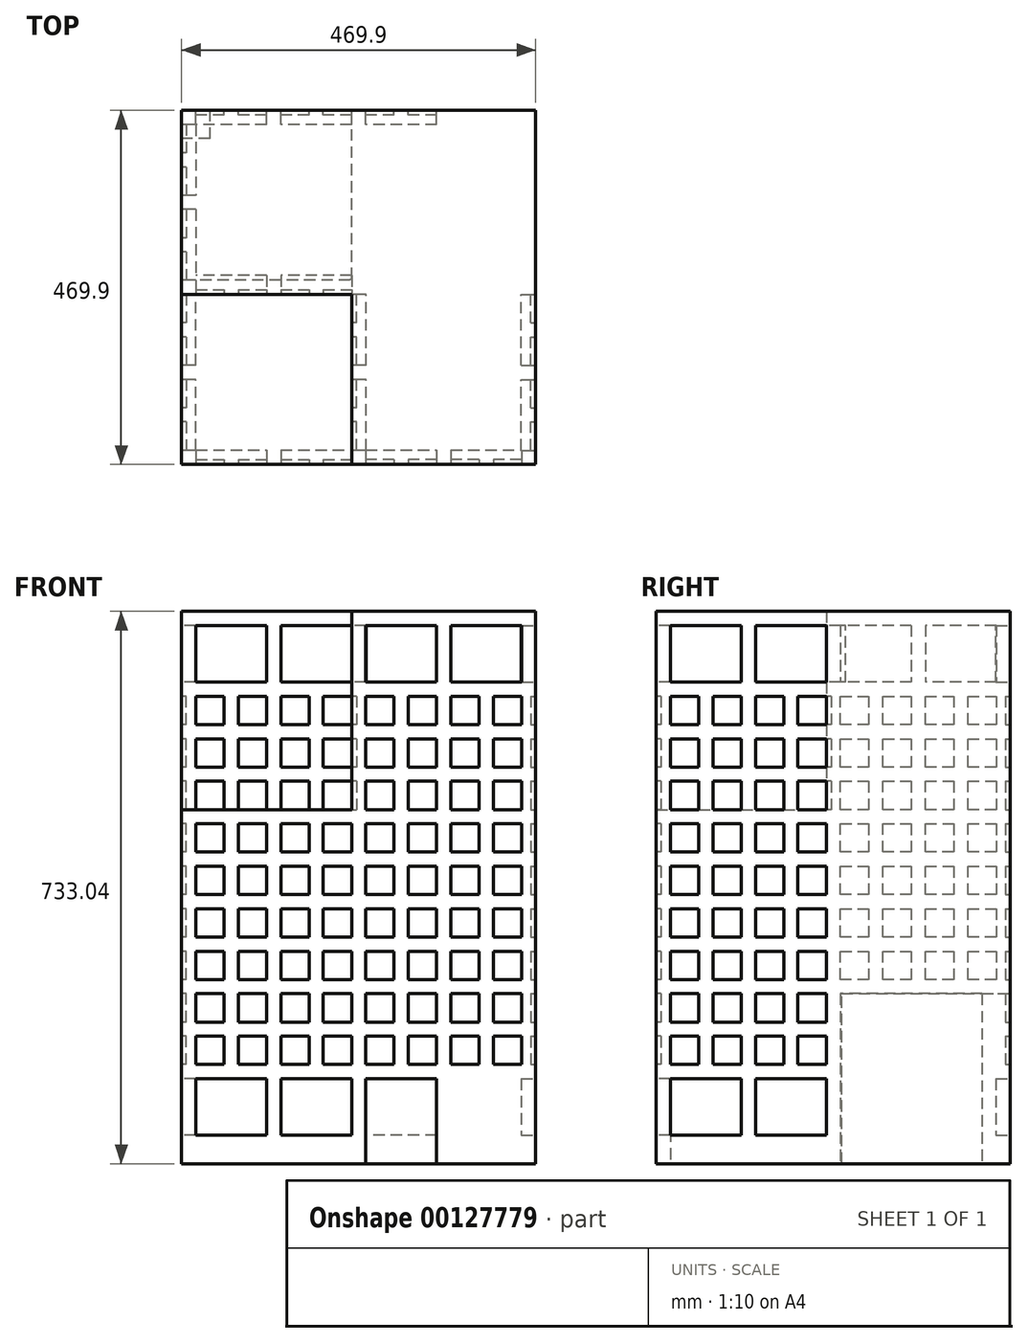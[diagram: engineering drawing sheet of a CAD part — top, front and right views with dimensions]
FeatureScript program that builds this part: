
annotation { "Feature Type Name" : "Feature", "Feature Type Description" : "" }
export const myFeature = defineFeature(function(context is Context, id is Id, definition is map)
    precondition{}
    {
        {
            var Q0;
            Q0=qCreatedBy(makeId("Front.planeOp"),FACE);
            var sketch = newSketch(context, id + "F0", { "sketchPlane" : qUnion([Q0])});
            skLineSegment(sketch, "E0", {"start": v(109.2, -466.79) * mm, "end": v(579.1, -466.79) * mm});
            skLineSegment(sketch, "E1", {"start": v(579.1, -466.79) * mm, "end": v(579.1, 303.85) * mm});
            skLineSegment(sketch, "E2", {"start": v(579.1, 303.85) * mm, "end": v(334.75, 303.85) * mm});
            skLineSegment(sketch, "E3", {"start": v(334.75, 303.85) * mm, "end": v(334.75, 21.9) * mm});
            skLineSegment(sketch, "E4", {"start": v(334.75, 21.9) * mm, "end": v(109.2, 21.9) * mm});
            skLineSegment(sketch, "E5", {"start": v(109.2, 21.9) * mm, "end": v(109.2, -466.79) * mm});
            skSolve(sketch);
        }
        {
            var Q0;
            {var subQ0=sQuery(id+"F0.wireOp",EDGE,"E1");Q0=makeQuery(id+"F0.imprint","IMPRINT",FACE,{"disambiguationData":[TD([[makeQuery(id+"F0.imprint","IMPRINT",EDGE,{"derivedFrom":subQ0}),1.0]])]});}
            extrude(context, id + "F1", {"entities" : qUnion([Q0]), "depth" : 469.9 * mm});
        }
        {
            var Q0;
            Q0=makeQuery(id+"F1.opExtrude","SWEPT_FACE",FACE,{"disambiguationData":[OSD([sQuery(id+"F0.wireOp",EDGE,"E4")])]});
            var sketch = newSketch(context, id + "F2", { "sketchPlane" : qUnion([Q0])});
            skLineSegment(sketch, "E6", {"start": v(104.7, -244.35) * mm, "end": v(339.26, -244.35) * mm});
            skSolve(sketch);
        }
        {
            var Q0;
            {var subQ1=sQuery(id+"F0.wireOp",EDGE,"E4");var subQ6=makeQuery(id+"F1.opExtrude","CAP_EDGE",EDGE,{"disambiguationData":[OSD([subQ1])],"isStart":true});Q0=makeQuery(id+"F2.imprint","IMPRINT",FACE,{"disambiguationData":[TD([[makeQuery(id+"F2.imprint","IMPRINT",EDGE,{"derivedFrom":subQ6}),1.0]])]});}
            extrude(context, id + "F3", {"entities" : qUnion([Q0]), "operationType" : NewBodyOperationType.ADD, "depth" : 281.94 * mm});
        }
        {
            var Q0;
            Q0=makeQuery(id+"F1.opExtrude","CAP_FACE",FACE,{"disambiguationData":[OSD([sQuery(id+"F0.wireOp",EDGE,"E0"),sQuery(id+"F0.wireOp",EDGE,"E1"),sQuery(id+"F0.wireOp",EDGE,"E2"),sQuery(id+"F0.wireOp",EDGE,"E3"),sQuery(id+"F0.wireOp",EDGE,"E4"),sQuery(id+"F0.wireOp",EDGE,"E5")])],"isStart":false});
            var sketch = newSketch(context, id + "F4", { "sketchPlane" : qUnion([Q0])});
            skLineSegment(sketch, "E7.bottom", {"start": v(128, -335.22) * mm, "end": v(221.98, -335.22) * mm});
            skLineSegment(sketch, "E7.top", {"start": v(128, -410.4) * mm, "end": v(221.98, -410.4) * mm});
            skLineSegment(sketch, "E7.left", {"start": v(128, -335.22) * mm, "end": v(128, -410.4) * mm});
            skLineSegment(sketch, "E7.right", {"start": v(221.98, -335.22) * mm, "end": v(221.98, -410.4) * mm});
            skLineSegment(sketch, "E8.1.0.0", {"start": v(240.77, -335.22) * mm, "end": v(334.75, -335.22) * mm});
            skLineSegment(sketch, "E8.1.0.1", {"start": v(334.75, -335.22) * mm, "end": v(334.75, -410.4) * mm});
            skLineSegment(sketch, "E8.1.0.2", {"start": v(240.77, -410.4) * mm, "end": v(334.75, -410.4) * mm});
            skLineSegment(sketch, "E8.1.0.3", {"start": v(240.77, -335.22) * mm, "end": v(240.77, -410.4) * mm});
            skLineSegment(sketch, "E8.2.0.0", {"start": v(353.55, -335.22) * mm, "end": v(447.53, -335.22) * mm});
            skLineSegment(sketch, "E8.2.0.1", {"start": v(447.53, -335.22) * mm, "end": v(447.53, -410.4) * mm});
            skLineSegment(sketch, "E8.2.0.3", {"start": v(353.55, -335.22) * mm, "end": v(353.55, -410.4) * mm});
            skLineSegment(sketch, "E8.direction1", {"start": v(128, -410.4) * mm, "end": v(240.77, -410.4) * mm, "construction": true});
            skLineSegment(sketch, "E9.bottom", {"start": v(522.71, -278.83) * mm, "end": v(560.3, -278.83) * mm});
            skLineSegment(sketch, "E9.top", {"start": v(522.71, -316.42) * mm, "end": v(560.3, -316.42) * mm});
            skLineSegment(sketch, "E9.left", {"start": v(522.71, -278.83) * mm, "end": v(522.71, -316.42) * mm});
            skLineSegment(sketch, "E9.right", {"start": v(560.3, -278.83) * mm, "end": v(560.3, -316.42) * mm});
            skLineSegment(sketch, "E10.0.1.0", {"start": v(522.71, -222.44) * mm, "end": v(560.3, -222.44) * mm});
            skLineSegment(sketch, "E10.0.1.1", {"start": v(560.3, -222.44) * mm, "end": v(560.3, -260.03) * mm});
            skLineSegment(sketch, "E10.0.1.2", {"start": v(522.71, -260.03) * mm, "end": v(560.3, -260.03) * mm});
            skLineSegment(sketch, "E10.0.1.3", {"start": v(522.71, -222.44) * mm, "end": v(522.71, -260.03) * mm});
            skLineSegment(sketch, "E10.0.2.0", {"start": v(522.71, -166.05) * mm, "end": v(560.3, -166.05) * mm});
            skLineSegment(sketch, "E10.0.2.1", {"start": v(560.3, -166.05) * mm, "end": v(560.3, -203.64) * mm});
            skLineSegment(sketch, "E10.0.2.2", {"start": v(522.71, -203.64) * mm, "end": v(560.3, -203.64) * mm});
            skLineSegment(sketch, "E10.0.2.3", {"start": v(522.71, -166.05) * mm, "end": v(522.71, -203.64) * mm});
            skLineSegment(sketch, "E10.0.3.0", {"start": v(522.71, -109.66) * mm, "end": v(560.3, -109.66) * mm});
            skLineSegment(sketch, "E10.0.3.1", {"start": v(560.3, -109.66) * mm, "end": v(560.3, -147.26) * mm});
            skLineSegment(sketch, "E10.0.3.2", {"start": v(522.71, -147.26) * mm, "end": v(560.3, -147.26) * mm});
            skLineSegment(sketch, "E10.0.3.3", {"start": v(522.71, -109.66) * mm, "end": v(522.71, -147.26) * mm});
            skLineSegment(sketch, "E10.0.4.0", {"start": v(522.71, -53.28) * mm, "end": v(560.3, -53.28) * mm});
            skLineSegment(sketch, "E10.0.4.1", {"start": v(560.3, -53.28) * mm, "end": v(560.3, -90.87) * mm});
            skLineSegment(sketch, "E10.0.4.2", {"start": v(522.71, -90.87) * mm, "end": v(560.3, -90.87) * mm});
            skLineSegment(sketch, "E10.0.4.3", {"start": v(522.71, -53.28) * mm, "end": v(522.71, -90.87) * mm});
            skLineSegment(sketch, "E10.0.5.0", {"start": v(522.71, 3.11) * mm, "end": v(560.3, 3.11) * mm});
            skLineSegment(sketch, "E10.0.5.1", {"start": v(560.3, 3.11) * mm, "end": v(560.3, -34.48) * mm});
            skLineSegment(sketch, "E10.0.5.2", {"start": v(522.71, -34.48) * mm, "end": v(560.3, -34.48) * mm});
            skLineSegment(sketch, "E10.0.5.3", {"start": v(522.71, 3.11) * mm, "end": v(522.71, -34.48) * mm});
            skLineSegment(sketch, "E10.1.0.0", {"start": v(466.33, -278.83) * mm, "end": v(503.92, -278.83) * mm});
            skLineSegment(sketch, "E10.1.0.1", {"start": v(503.92, -278.83) * mm, "end": v(503.92, -316.42) * mm});
            skLineSegment(sketch, "E10.1.0.2", {"start": v(466.33, -316.42) * mm, "end": v(503.92, -316.42) * mm});
            skLineSegment(sketch, "E10.1.0.3", {"start": v(466.33, -278.83) * mm, "end": v(466.33, -316.42) * mm});
            skLineSegment(sketch, "E10.1.1.0", {"start": v(466.33, -222.44) * mm, "end": v(503.92, -222.44) * mm});
            skLineSegment(sketch, "E10.1.1.1", {"start": v(503.92, -222.44) * mm, "end": v(503.92, -260.03) * mm});
            skLineSegment(sketch, "E10.1.1.2", {"start": v(466.33, -260.03) * mm, "end": v(503.92, -260.03) * mm});
            skLineSegment(sketch, "E10.1.1.3", {"start": v(466.33, -222.44) * mm, "end": v(466.33, -260.03) * mm});
            skLineSegment(sketch, "E10.1.2.0", {"start": v(466.33, -166.05) * mm, "end": v(503.92, -166.05) * mm});
            skLineSegment(sketch, "E10.1.2.1", {"start": v(503.92, -166.05) * mm, "end": v(503.92, -203.64) * mm});
            skLineSegment(sketch, "E10.1.2.2", {"start": v(466.33, -203.64) * mm, "end": v(503.92, -203.64) * mm});
            skLineSegment(sketch, "E10.1.2.3", {"start": v(466.33, -166.05) * mm, "end": v(466.33, -203.64) * mm});
            skLineSegment(sketch, "E10.1.3.0", {"start": v(466.33, -109.66) * mm, "end": v(503.92, -109.66) * mm});
            skLineSegment(sketch, "E10.1.3.1", {"start": v(503.92, -109.66) * mm, "end": v(503.92, -147.26) * mm});
            skLineSegment(sketch, "E10.1.3.2", {"start": v(466.33, -147.26) * mm, "end": v(503.92, -147.26) * mm});
            skLineSegment(sketch, "E10.1.3.3", {"start": v(466.33, -109.66) * mm, "end": v(466.33, -147.26) * mm});
            skLineSegment(sketch, "E10.1.4.0", {"start": v(466.33, -53.28) * mm, "end": v(503.92, -53.28) * mm});
            skLineSegment(sketch, "E10.1.4.1", {"start": v(503.92, -53.28) * mm, "end": v(503.92, -90.87) * mm});
            skLineSegment(sketch, "E10.1.4.2", {"start": v(466.33, -90.87) * mm, "end": v(503.92, -90.87) * mm});
            skLineSegment(sketch, "E10.1.4.3", {"start": v(466.33, -53.28) * mm, "end": v(466.33, -90.87) * mm});
            skLineSegment(sketch, "E10.1.5.0", {"start": v(466.33, 3.11) * mm, "end": v(503.92, 3.11) * mm});
            skLineSegment(sketch, "E10.1.5.1", {"start": v(503.92, 3.11) * mm, "end": v(503.92, -34.48) * mm});
            skLineSegment(sketch, "E10.1.5.2", {"start": v(466.33, -34.48) * mm, "end": v(503.92, -34.48) * mm});
            skLineSegment(sketch, "E10.1.5.3", {"start": v(466.33, 3.11) * mm, "end": v(466.33, -34.48) * mm});
            skLineSegment(sketch, "E10.2.0.0", {"start": v(409.94, -278.83) * mm, "end": v(447.53, -278.83) * mm});
            skLineSegment(sketch, "E10.2.0.1", {"start": v(447.53, -278.83) * mm, "end": v(447.53, -316.42) * mm});
            skLineSegment(sketch, "E10.2.0.2", {"start": v(409.94, -316.42) * mm, "end": v(447.53, -316.42) * mm});
            skLineSegment(sketch, "E10.2.0.3", {"start": v(409.94, -278.83) * mm, "end": v(409.94, -316.42) * mm});
            skLineSegment(sketch, "E10.2.1.0", {"start": v(409.94, -222.44) * mm, "end": v(447.53, -222.44) * mm});
            skLineSegment(sketch, "E10.2.1.1", {"start": v(447.53, -222.44) * mm, "end": v(447.53, -260.03) * mm});
            skLineSegment(sketch, "E10.2.1.2", {"start": v(409.94, -260.03) * mm, "end": v(447.53, -260.03) * mm});
            skLineSegment(sketch, "E10.2.1.3", {"start": v(409.94, -222.44) * mm, "end": v(409.94, -260.03) * mm});
            skLineSegment(sketch, "E10.2.2.0", {"start": v(409.94, -166.05) * mm, "end": v(447.53, -166.05) * mm});
            skLineSegment(sketch, "E10.2.2.1", {"start": v(447.53, -166.05) * mm, "end": v(447.53, -203.64) * mm});
            skLineSegment(sketch, "E10.2.2.2", {"start": v(409.94, -203.64) * mm, "end": v(447.53, -203.64) * mm});
            skLineSegment(sketch, "E10.2.2.3", {"start": v(409.94, -166.05) * mm, "end": v(409.94, -203.64) * mm});
            skLineSegment(sketch, "E10.2.3.0", {"start": v(409.94, -109.66) * mm, "end": v(447.53, -109.66) * mm});
            skLineSegment(sketch, "E10.2.3.1", {"start": v(447.53, -109.66) * mm, "end": v(447.53, -147.26) * mm});
            skLineSegment(sketch, "E10.2.3.2", {"start": v(409.94, -147.26) * mm, "end": v(447.53, -147.26) * mm});
            skLineSegment(sketch, "E10.2.3.3", {"start": v(409.94, -109.66) * mm, "end": v(409.94, -147.26) * mm});
            skLineSegment(sketch, "E10.2.4.0", {"start": v(409.94, -53.28) * mm, "end": v(447.53, -53.28) * mm});
            skLineSegment(sketch, "E10.2.4.1", {"start": v(447.53, -53.28) * mm, "end": v(447.53, -90.87) * mm});
            skLineSegment(sketch, "E10.2.4.2", {"start": v(409.94, -90.87) * mm, "end": v(447.53, -90.87) * mm});
            skLineSegment(sketch, "E10.2.4.3", {"start": v(409.94, -53.28) * mm, "end": v(409.94, -90.87) * mm});
            skLineSegment(sketch, "E10.2.5.0", {"start": v(409.94, 3.11) * mm, "end": v(447.53, 3.11) * mm});
            skLineSegment(sketch, "E10.2.5.1", {"start": v(447.53, 3.11) * mm, "end": v(447.53, -34.48) * mm});
            skLineSegment(sketch, "E10.2.5.2", {"start": v(409.94, -34.48) * mm, "end": v(447.53, -34.48) * mm});
            skLineSegment(sketch, "E10.2.5.3", {"start": v(409.94, 3.11) * mm, "end": v(409.94, -34.48) * mm});
            skLineSegment(sketch, "E10.3.0.0", {"start": v(353.55, -278.83) * mm, "end": v(391.14, -278.83) * mm});
            skLineSegment(sketch, "E10.3.0.1", {"start": v(391.14, -278.83) * mm, "end": v(391.14, -316.42) * mm});
            skLineSegment(sketch, "E10.3.0.2", {"start": v(353.55, -316.42) * mm, "end": v(391.14, -316.42) * mm});
            skLineSegment(sketch, "E10.3.0.3", {"start": v(353.55, -278.83) * mm, "end": v(353.55, -316.42) * mm});
            skLineSegment(sketch, "E10.3.1.0", {"start": v(353.55, -222.44) * mm, "end": v(391.14, -222.44) * mm});
            skLineSegment(sketch, "E10.3.1.1", {"start": v(391.14, -222.44) * mm, "end": v(391.14, -260.03) * mm});
            skLineSegment(sketch, "E10.3.1.2", {"start": v(353.55, -260.03) * mm, "end": v(391.14, -260.03) * mm});
            skLineSegment(sketch, "E10.3.1.3", {"start": v(353.55, -222.44) * mm, "end": v(353.55, -260.03) * mm});
            skLineSegment(sketch, "E10.3.2.0", {"start": v(353.55, -166.05) * mm, "end": v(391.14, -166.05) * mm});
            skLineSegment(sketch, "E10.3.2.1", {"start": v(391.14, -166.05) * mm, "end": v(391.14, -203.64) * mm});
            skLineSegment(sketch, "E10.3.2.2", {"start": v(353.55, -203.64) * mm, "end": v(391.14, -203.64) * mm});
            skLineSegment(sketch, "E10.3.2.3", {"start": v(353.55, -166.05) * mm, "end": v(353.55, -203.64) * mm});
            skLineSegment(sketch, "E10.3.3.0", {"start": v(353.55, -109.66) * mm, "end": v(391.14, -109.66) * mm});
            skLineSegment(sketch, "E10.3.3.1", {"start": v(391.14, -109.66) * mm, "end": v(391.14, -147.26) * mm});
            skLineSegment(sketch, "E10.3.3.2", {"start": v(353.55, -147.26) * mm, "end": v(391.14, -147.26) * mm});
            skLineSegment(sketch, "E10.3.3.3", {"start": v(353.55, -109.66) * mm, "end": v(353.55, -147.26) * mm});
            skLineSegment(sketch, "E10.3.4.0", {"start": v(353.55, -53.28) * mm, "end": v(391.14, -53.28) * mm});
            skLineSegment(sketch, "E10.3.4.1", {"start": v(391.14, -53.28) * mm, "end": v(391.14, -90.87) * mm});
            skLineSegment(sketch, "E10.3.4.2", {"start": v(353.55, -90.87) * mm, "end": v(391.14, -90.87) * mm});
            skLineSegment(sketch, "E10.3.4.3", {"start": v(353.55, -53.28) * mm, "end": v(353.55, -90.87) * mm});
            skLineSegment(sketch, "E10.3.5.0", {"start": v(353.55, 3.11) * mm, "end": v(391.14, 3.11) * mm});
            skLineSegment(sketch, "E10.3.5.1", {"start": v(391.14, 3.11) * mm, "end": v(391.14, -34.48) * mm});
            skLineSegment(sketch, "E10.3.5.2", {"start": v(353.55, -34.48) * mm, "end": v(391.14, -34.48) * mm});
            skLineSegment(sketch, "E10.3.5.3", {"start": v(353.55, 3.11) * mm, "end": v(353.55, -34.48) * mm});
            skLineSegment(sketch, "E10.4.0.0", {"start": v(297.16, -278.83) * mm, "end": v(334.75, -278.83) * mm});
            skLineSegment(sketch, "E10.4.0.1", {"start": v(334.75, -278.83) * mm, "end": v(334.75, -316.42) * mm});
            skLineSegment(sketch, "E10.4.0.2", {"start": v(297.16, -316.42) * mm, "end": v(334.75, -316.42) * mm});
            skLineSegment(sketch, "E10.4.0.3", {"start": v(297.16, -278.83) * mm, "end": v(297.16, -316.42) * mm});
            skLineSegment(sketch, "E10.4.1.0", {"start": v(297.16, -222.44) * mm, "end": v(334.75, -222.44) * mm});
            skLineSegment(sketch, "E10.4.1.1", {"start": v(334.75, -222.44) * mm, "end": v(334.75, -260.03) * mm});
            skLineSegment(sketch, "E10.4.1.2", {"start": v(297.16, -260.03) * mm, "end": v(334.75, -260.03) * mm});
            skLineSegment(sketch, "E10.4.1.3", {"start": v(297.16, -222.44) * mm, "end": v(297.16, -260.03) * mm});
            skLineSegment(sketch, "E10.4.2.0", {"start": v(297.16, -166.05) * mm, "end": v(334.75, -166.05) * mm});
            skLineSegment(sketch, "E10.4.2.1", {"start": v(334.75, -166.05) * mm, "end": v(334.75, -203.64) * mm});
            skLineSegment(sketch, "E10.4.2.2", {"start": v(297.16, -203.64) * mm, "end": v(334.75, -203.64) * mm});
            skLineSegment(sketch, "E10.4.2.3", {"start": v(297.16, -166.05) * mm, "end": v(297.16, -203.64) * mm});
            skLineSegment(sketch, "E10.4.3.0", {"start": v(297.16, -109.66) * mm, "end": v(334.75, -109.66) * mm});
            skLineSegment(sketch, "E10.4.3.1", {"start": v(334.75, -109.66) * mm, "end": v(334.75, -147.26) * mm});
            skLineSegment(sketch, "E10.4.3.2", {"start": v(297.16, -147.26) * mm, "end": v(334.75, -147.26) * mm});
            skLineSegment(sketch, "E10.4.3.3", {"start": v(297.16, -109.66) * mm, "end": v(297.16, -147.26) * mm});
            skLineSegment(sketch, "E10.4.4.0", {"start": v(297.16, -53.28) * mm, "end": v(334.75, -53.28) * mm});
            skLineSegment(sketch, "E10.4.4.1", {"start": v(334.75, -53.28) * mm, "end": v(334.75, -90.87) * mm});
            skLineSegment(sketch, "E10.4.4.2", {"start": v(297.16, -90.87) * mm, "end": v(334.75, -90.87) * mm});
            skLineSegment(sketch, "E10.4.4.3", {"start": v(297.16, -53.28) * mm, "end": v(297.16, -90.87) * mm});
            skLineSegment(sketch, "E10.4.5.0", {"start": v(297.16, 3.11) * mm, "end": v(334.75, 3.11) * mm});
            skLineSegment(sketch, "E10.4.5.1", {"start": v(334.75, 3.11) * mm, "end": v(334.75, -34.48) * mm});
            skLineSegment(sketch, "E10.4.5.2", {"start": v(297.16, -34.48) * mm, "end": v(334.75, -34.48) * mm});
            skLineSegment(sketch, "E10.4.5.3", {"start": v(297.16, 3.11) * mm, "end": v(297.16, -34.48) * mm});
            skLineSegment(sketch, "E10.5.0.0", {"start": v(240.77, -278.83) * mm, "end": v(278.37, -278.83) * mm});
            skLineSegment(sketch, "E10.5.0.1", {"start": v(278.37, -278.83) * mm, "end": v(278.37, -316.42) * mm});
            skLineSegment(sketch, "E10.5.0.2", {"start": v(240.77, -316.42) * mm, "end": v(278.37, -316.42) * mm});
            skLineSegment(sketch, "E10.5.0.3", {"start": v(240.77, -278.83) * mm, "end": v(240.77, -316.42) * mm});
            skLineSegment(sketch, "E10.5.1.0", {"start": v(240.77, -222.44) * mm, "end": v(278.37, -222.44) * mm});
            skLineSegment(sketch, "E10.5.1.1", {"start": v(278.37, -222.44) * mm, "end": v(278.37, -260.03) * mm});
            skLineSegment(sketch, "E10.5.1.2", {"start": v(240.77, -260.03) * mm, "end": v(278.37, -260.03) * mm});
            skLineSegment(sketch, "E10.5.1.3", {"start": v(240.77, -222.44) * mm, "end": v(240.77, -260.03) * mm});
            skLineSegment(sketch, "E10.5.2.0", {"start": v(240.77, -166.05) * mm, "end": v(278.37, -166.05) * mm});
            skLineSegment(sketch, "E10.5.2.1", {"start": v(278.37, -166.05) * mm, "end": v(278.37, -203.64) * mm});
            skLineSegment(sketch, "E10.5.2.2", {"start": v(240.77, -203.64) * mm, "end": v(278.37, -203.64) * mm});
            skLineSegment(sketch, "E10.5.2.3", {"start": v(240.77, -166.05) * mm, "end": v(240.77, -203.64) * mm});
            skLineSegment(sketch, "E10.5.3.0", {"start": v(240.77, -109.66) * mm, "end": v(278.37, -109.66) * mm});
            skLineSegment(sketch, "E10.5.3.1", {"start": v(278.37, -109.66) * mm, "end": v(278.37, -147.26) * mm});
            skLineSegment(sketch, "E10.5.3.2", {"start": v(240.77, -147.26) * mm, "end": v(278.37, -147.26) * mm});
            skLineSegment(sketch, "E10.5.3.3", {"start": v(240.77, -109.66) * mm, "end": v(240.77, -147.26) * mm});
            skLineSegment(sketch, "E10.5.4.0", {"start": v(240.77, -53.28) * mm, "end": v(278.37, -53.28) * mm});
            skLineSegment(sketch, "E10.5.4.1", {"start": v(278.37, -53.28) * mm, "end": v(278.37, -90.87) * mm});
            skLineSegment(sketch, "E10.5.4.2", {"start": v(240.77, -90.87) * mm, "end": v(278.37, -90.87) * mm});
            skLineSegment(sketch, "E10.5.4.3", {"start": v(240.77, -53.28) * mm, "end": v(240.77, -90.87) * mm});
            skLineSegment(sketch, "E10.5.5.0", {"start": v(240.77, 3.11) * mm, "end": v(278.37, 3.11) * mm});
            skLineSegment(sketch, "E10.5.5.1", {"start": v(278.37, 3.11) * mm, "end": v(278.37, -34.48) * mm});
            skLineSegment(sketch, "E10.5.5.2", {"start": v(240.77, -34.48) * mm, "end": v(278.37, -34.48) * mm});
            skLineSegment(sketch, "E10.5.5.3", {"start": v(240.77, 3.11) * mm, "end": v(240.77, -34.48) * mm});
            skLineSegment(sketch, "E10.6.0.0", {"start": v(184.39, -278.83) * mm, "end": v(221.98, -278.83) * mm});
            skLineSegment(sketch, "E10.6.0.1", {"start": v(221.98, -278.83) * mm, "end": v(221.98, -316.42) * mm});
            skLineSegment(sketch, "E10.6.0.2", {"start": v(184.39, -316.42) * mm, "end": v(221.98, -316.42) * mm});
            skLineSegment(sketch, "E10.6.0.3", {"start": v(184.39, -278.83) * mm, "end": v(184.39, -316.42) * mm});
            skLineSegment(sketch, "E10.6.1.0", {"start": v(184.39, -222.44) * mm, "end": v(221.98, -222.44) * mm});
            skLineSegment(sketch, "E10.6.1.1", {"start": v(221.98, -222.44) * mm, "end": v(221.98, -260.03) * mm});
            skLineSegment(sketch, "E10.6.1.2", {"start": v(184.39, -260.03) * mm, "end": v(221.98, -260.03) * mm});
            skLineSegment(sketch, "E10.6.1.3", {"start": v(184.39, -222.44) * mm, "end": v(184.39, -260.03) * mm});
            skLineSegment(sketch, "E10.6.2.0", {"start": v(184.39, -166.05) * mm, "end": v(221.98, -166.05) * mm});
            skLineSegment(sketch, "E10.6.2.1", {"start": v(221.98, -166.05) * mm, "end": v(221.98, -203.64) * mm});
            skLineSegment(sketch, "E10.6.2.2", {"start": v(184.39, -203.64) * mm, "end": v(221.98, -203.64) * mm});
            skLineSegment(sketch, "E10.6.2.3", {"start": v(184.39, -166.05) * mm, "end": v(184.39, -203.64) * mm});
            skLineSegment(sketch, "E10.6.3.0", {"start": v(184.39, -109.66) * mm, "end": v(221.98, -109.66) * mm});
            skLineSegment(sketch, "E10.6.3.1", {"start": v(221.98, -109.66) * mm, "end": v(221.98, -147.26) * mm});
            skLineSegment(sketch, "E10.6.3.2", {"start": v(184.39, -147.26) * mm, "end": v(221.98, -147.26) * mm});
            skLineSegment(sketch, "E10.6.3.3", {"start": v(184.39, -109.66) * mm, "end": v(184.39, -147.26) * mm});
            skLineSegment(sketch, "E10.6.4.0", {"start": v(184.39, -53.28) * mm, "end": v(221.98, -53.28) * mm});
            skLineSegment(sketch, "E10.6.4.1", {"start": v(221.98, -53.28) * mm, "end": v(221.98, -90.87) * mm});
            skLineSegment(sketch, "E10.6.4.2", {"start": v(184.39, -90.87) * mm, "end": v(221.98, -90.87) * mm});
            skLineSegment(sketch, "E10.6.4.3", {"start": v(184.39, -53.28) * mm, "end": v(184.39, -90.87) * mm});
            skLineSegment(sketch, "E10.6.5.0", {"start": v(184.39, 3.11) * mm, "end": v(221.98, 3.11) * mm});
            skLineSegment(sketch, "E10.6.5.1", {"start": v(221.98, 3.11) * mm, "end": v(221.98, -34.48) * mm});
            skLineSegment(sketch, "E10.6.5.2", {"start": v(184.39, -34.48) * mm, "end": v(221.98, -34.48) * mm});
            skLineSegment(sketch, "E10.6.5.3", {"start": v(184.39, 3.11) * mm, "end": v(184.39, -34.48) * mm});
            skLineSegment(sketch, "E10.7.0.0", {"start": v(128, -278.83) * mm, "end": v(165.59, -278.83) * mm});
            skLineSegment(sketch, "E10.7.0.1", {"start": v(165.59, -278.83) * mm, "end": v(165.59, -316.42) * mm});
            skLineSegment(sketch, "E10.7.0.2", {"start": v(128, -316.42) * mm, "end": v(165.59, -316.42) * mm});
            skLineSegment(sketch, "E10.7.0.3", {"start": v(128, -278.83) * mm, "end": v(128, -316.42) * mm});
            skLineSegment(sketch, "E10.7.1.0", {"start": v(128, -222.44) * mm, "end": v(165.59, -222.44) * mm});
            skLineSegment(sketch, "E10.7.1.1", {"start": v(165.59, -222.44) * mm, "end": v(165.59, -260.03) * mm});
            skLineSegment(sketch, "E10.7.1.2", {"start": v(128, -260.03) * mm, "end": v(165.59, -260.03) * mm});
            skLineSegment(sketch, "E10.7.1.3", {"start": v(128, -222.44) * mm, "end": v(128, -260.03) * mm});
            skLineSegment(sketch, "E10.7.2.0", {"start": v(128, -166.05) * mm, "end": v(165.59, -166.05) * mm});
            skLineSegment(sketch, "E10.7.2.1", {"start": v(165.59, -166.05) * mm, "end": v(165.59, -203.64) * mm});
            skLineSegment(sketch, "E10.7.2.2", {"start": v(128, -203.64) * mm, "end": v(165.59, -203.64) * mm});
            skLineSegment(sketch, "E10.7.2.3", {"start": v(128, -166.05) * mm, "end": v(128, -203.64) * mm});
            skLineSegment(sketch, "E10.7.3.0", {"start": v(128, -109.66) * mm, "end": v(165.59, -109.66) * mm});
            skLineSegment(sketch, "E10.7.3.1", {"start": v(165.59, -109.66) * mm, "end": v(165.59, -147.26) * mm});
            skLineSegment(sketch, "E10.7.3.2", {"start": v(128, -147.26) * mm, "end": v(165.59, -147.26) * mm});
            skLineSegment(sketch, "E10.7.3.3", {"start": v(128, -109.66) * mm, "end": v(128, -147.26) * mm});
            skLineSegment(sketch, "E10.7.4.0", {"start": v(128, -53.28) * mm, "end": v(165.59, -53.28) * mm});
            skLineSegment(sketch, "E10.7.4.1", {"start": v(165.59, -53.28) * mm, "end": v(165.59, -90.87) * mm});
            skLineSegment(sketch, "E10.7.4.2", {"start": v(128, -90.87) * mm, "end": v(165.59, -90.87) * mm});
            skLineSegment(sketch, "E10.7.4.3", {"start": v(128, -53.28) * mm, "end": v(128, -90.87) * mm});
            skLineSegment(sketch, "E10.7.5.0", {"start": v(128, 3.11) * mm, "end": v(165.59, 3.11) * mm});
            skLineSegment(sketch, "E10.7.5.1", {"start": v(165.59, 3.11) * mm, "end": v(165.59, -34.48) * mm});
            skLineSegment(sketch, "E10.7.5.2", {"start": v(128, -34.48) * mm, "end": v(165.59, -34.48) * mm});
            skLineSegment(sketch, "E10.7.5.3", {"start": v(128, 3.11) * mm, "end": v(128, -34.48) * mm});
            skLineSegment(sketch, "E10.direction1", {"start": v(522.71, -316.42) * mm, "end": v(466.33, -316.42) * mm, "construction": true});
            skLineSegment(sketch, "E10.direction2", {"start": v(522.71, -316.42) * mm, "end": v(522.71, -260.03) * mm, "construction": true});
            skLineSegment(sketch, "E11.bottom", {"start": v(466.33, 266.26) * mm, "end": v(560.3, 266.26) * mm});
            skLineSegment(sketch, "E11.top", {"start": v(466.33, 191.07) * mm, "end": v(560.3, 191.07) * mm});
            skLineSegment(sketch, "E11.left", {"start": v(466.33, 266.26) * mm, "end": v(466.33, 191.07) * mm});
            skLineSegment(sketch, "E11.right", {"start": v(560.3, 266.26) * mm, "end": v(560.3, 191.07) * mm});
            skLineSegment(sketch, "E12.bottom", {"start": v(353.55, 266.26) * mm, "end": v(447.53, 266.26) * mm});
            skLineSegment(sketch, "E12.top", {"start": v(353.55, 191.07) * mm, "end": v(447.53, 191.07) * mm});
            skLineSegment(sketch, "E12.left", {"start": v(353.55, 266.26) * mm, "end": v(353.55, 191.07) * mm});
            skLineSegment(sketch, "E12.right", {"start": v(447.53, 266.26) * mm, "end": v(447.53, 191.07) * mm});
            skLineSegment(sketch, "E13.bottom", {"start": v(560.3, 59.5) * mm, "end": v(522.71, 59.5) * mm});
            skLineSegment(sketch, "E13.top", {"start": v(560.3, 21.9) * mm, "end": v(522.71, 21.9) * mm});
            skLineSegment(sketch, "E13.left", {"start": v(560.3, 59.5) * mm, "end": v(560.3, 21.9) * mm});
            skLineSegment(sketch, "E13.right", {"start": v(522.71, 59.5) * mm, "end": v(522.71, 21.9) * mm});
            skLineSegment(sketch, "E14.0.1.0", {"start": v(560.3, 115.89) * mm, "end": v(522.71, 115.89) * mm});
            skLineSegment(sketch, "E14.0.1.1", {"start": v(560.3, 115.89) * mm, "end": v(560.3, 78.3) * mm});
            skLineSegment(sketch, "E14.0.1.2", {"start": v(560.3, 78.3) * mm, "end": v(522.71, 78.3) * mm});
            skLineSegment(sketch, "E14.0.1.3", {"start": v(522.71, 115.89) * mm, "end": v(522.71, 78.3) * mm});
            skLineSegment(sketch, "E14.0.2.0", {"start": v(560.3, 172.28) * mm, "end": v(522.71, 172.28) * mm});
            skLineSegment(sketch, "E14.0.2.1", {"start": v(560.3, 172.28) * mm, "end": v(560.3, 134.68) * mm});
            skLineSegment(sketch, "E14.0.2.2", {"start": v(560.3, 134.68) * mm, "end": v(522.71, 134.68) * mm});
            skLineSegment(sketch, "E14.0.2.3", {"start": v(522.71, 172.28) * mm, "end": v(522.71, 134.68) * mm});
            skLineSegment(sketch, "E14.1.0.0", {"start": v(503.92, 59.5) * mm, "end": v(466.33, 59.5) * mm});
            skLineSegment(sketch, "E14.1.0.1", {"start": v(503.92, 59.5) * mm, "end": v(503.92, 21.9) * mm});
            skLineSegment(sketch, "E14.1.0.2", {"start": v(503.92, 21.9) * mm, "end": v(466.33, 21.9) * mm});
            skLineSegment(sketch, "E14.1.0.3", {"start": v(466.33, 59.5) * mm, "end": v(466.33, 21.9) * mm});
            skLineSegment(sketch, "E14.1.1.0", {"start": v(503.92, 115.89) * mm, "end": v(466.33, 115.89) * mm});
            skLineSegment(sketch, "E14.1.1.1", {"start": v(503.92, 115.89) * mm, "end": v(503.92, 78.3) * mm});
            skLineSegment(sketch, "E14.1.1.2", {"start": v(503.92, 78.3) * mm, "end": v(466.33, 78.3) * mm});
            skLineSegment(sketch, "E14.1.1.3", {"start": v(466.33, 115.89) * mm, "end": v(466.33, 78.3) * mm});
            skLineSegment(sketch, "E14.1.2.0", {"start": v(503.92, 172.28) * mm, "end": v(466.33, 172.28) * mm});
            skLineSegment(sketch, "E14.1.2.1", {"start": v(503.92, 172.28) * mm, "end": v(503.92, 134.68) * mm});
            skLineSegment(sketch, "E14.1.2.2", {"start": v(503.92, 134.68) * mm, "end": v(466.33, 134.68) * mm});
            skLineSegment(sketch, "E14.1.2.3", {"start": v(466.33, 172.28) * mm, "end": v(466.33, 134.68) * mm});
            skLineSegment(sketch, "E14.2.0.0", {"start": v(447.53, 59.5) * mm, "end": v(409.94, 59.5) * mm});
            skLineSegment(sketch, "E14.2.0.1", {"start": v(447.53, 59.5) * mm, "end": v(447.53, 21.9) * mm});
            skLineSegment(sketch, "E14.2.0.2", {"start": v(447.53, 21.9) * mm, "end": v(409.94, 21.9) * mm});
            skLineSegment(sketch, "E14.2.0.3", {"start": v(409.94, 59.5) * mm, "end": v(409.94, 21.9) * mm});
            skLineSegment(sketch, "E14.2.1.0", {"start": v(447.53, 115.89) * mm, "end": v(409.94, 115.89) * mm});
            skLineSegment(sketch, "E14.2.1.1", {"start": v(447.53, 115.89) * mm, "end": v(447.53, 78.3) * mm});
            skLineSegment(sketch, "E14.2.1.2", {"start": v(447.53, 78.3) * mm, "end": v(409.94, 78.3) * mm});
            skLineSegment(sketch, "E14.2.1.3", {"start": v(409.94, 115.89) * mm, "end": v(409.94, 78.3) * mm});
            skLineSegment(sketch, "E14.2.2.0", {"start": v(447.53, 172.28) * mm, "end": v(409.94, 172.28) * mm});
            skLineSegment(sketch, "E14.2.2.1", {"start": v(447.53, 172.28) * mm, "end": v(447.53, 134.68) * mm});
            skLineSegment(sketch, "E14.2.2.2", {"start": v(447.53, 134.68) * mm, "end": v(409.94, 134.68) * mm});
            skLineSegment(sketch, "E14.2.2.3", {"start": v(409.94, 172.28) * mm, "end": v(409.94, 134.68) * mm});
            skLineSegment(sketch, "E14.3.0.0", {"start": v(391.14, 59.5) * mm, "end": v(353.55, 59.5) * mm});
            skLineSegment(sketch, "E14.3.0.1", {"start": v(391.14, 59.5) * mm, "end": v(391.14, 21.9) * mm});
            skLineSegment(sketch, "E14.3.0.2", {"start": v(391.14, 21.9) * mm, "end": v(353.55, 21.9) * mm});
            skLineSegment(sketch, "E14.3.0.3", {"start": v(353.55, 59.5) * mm, "end": v(353.55, 21.9) * mm});
            skLineSegment(sketch, "E14.3.1.0", {"start": v(391.14, 115.89) * mm, "end": v(353.55, 115.89) * mm});
            skLineSegment(sketch, "E14.3.1.1", {"start": v(391.14, 115.89) * mm, "end": v(391.14, 78.3) * mm});
            skLineSegment(sketch, "E14.3.1.2", {"start": v(391.14, 78.3) * mm, "end": v(353.55, 78.3) * mm});
            skLineSegment(sketch, "E14.3.1.3", {"start": v(353.55, 115.89) * mm, "end": v(353.55, 78.3) * mm});
            skLineSegment(sketch, "E14.3.2.0", {"start": v(391.14, 172.28) * mm, "end": v(353.55, 172.28) * mm});
            skLineSegment(sketch, "E14.3.2.1", {"start": v(391.14, 172.28) * mm, "end": v(391.14, 134.68) * mm});
            skLineSegment(sketch, "E14.3.2.2", {"start": v(391.14, 134.68) * mm, "end": v(353.55, 134.68) * mm});
            skLineSegment(sketch, "E14.3.2.3", {"start": v(353.55, 172.28) * mm, "end": v(353.55, 134.68) * mm});
            skLineSegment(sketch, "E14.direction1", {"start": v(522.71, 21.9) * mm, "end": v(466.33, 21.9) * mm, "construction": true});
            skLineSegment(sketch, "E14.direction2", {"start": v(522.71, 21.9) * mm, "end": v(522.71, 78.3) * mm, "construction": true});
            skLineSegment(sketch, "E15", {"start": v(353.55, -410.4) * mm, "end": v(353.55, -466.79) * mm});
            skLineSegment(sketch, "E16", {"start": v(447.53, -410.4) * mm, "end": v(447.53, -466.79) * mm});
            skSolve(sketch);
        }
        {
            var Q0;
            Q0=makeQuery(id+"F4.imprint","IMPRINT",FACE,{"disambiguationData":[TD([[makeQuery(id+"F4.imprint","IMPRINT",EDGE,{"derivedFrom":sQuery(id+"F4.wireOp",EDGE,"E12.bottom")}),-1.0]])]});
            var Q1;
            Q1=makeQuery(id+"F4.imprint","IMPRINT",FACE,{"disambiguationData":[TD([[makeQuery(id+"F4.imprint","IMPRINT",EDGE,{"derivedFrom":sQuery(id+"F4.wireOp",EDGE,"E11.bottom")}),-1.0]])]});
            var Q2;
            Q2=makeQuery(id+"F4.imprint","IMPRINT",FACE,{"disambiguationData":[TD([[makeQuery(id+"F4.imprint","IMPRINT",EDGE,{"derivedFrom":sQuery(id+"F4.wireOp",EDGE,"E8.2.0.0")}),-1.0]])]});
            var Q3;
            Q3=makeQuery(id+"F4.imprint","IMPRINT",FACE,{"disambiguationData":[TD([[makeQuery(id+"F4.imprint","IMPRINT",EDGE,{"derivedFrom":sQuery(id+"F4.wireOp",EDGE,"E8.1.0.0")}),-1.0]])]});
            var Q4;
            Q4=makeQuery(id+"F4.imprint","IMPRINT",FACE,{"disambiguationData":[TD([[makeQuery(id+"F4.imprint","IMPRINT",EDGE,{"derivedFrom":sQuery(id+"F4.wireOp",EDGE,"E7.bottom")}),-1.0]])]});
            extrude(context, id + "F5", {"entities" : qUnion([Q0, Q1, Q2, Q3, Q4]), "operationType" : NewBodyOperationType.REMOVE, "oppositeDirection" : true, "depth" : 19.05 * mm});
        }
        {
            var Q0;
            Q0 = qSketchRegion(id + "F4", true);
            extrude(context, id + "F6", {"entities" : qUnion([Q0]), "operationType" : NewBodyOperationType.REMOVE, "oppositeDirection" : true, "depth" : 6.35 * mm});
        }
        {
            var Q0;
            Q0=makeQuery(id+"F1.opExtrude","CAP_FACE",FACE,{"disambiguationData":[OSD([sQuery(id+"F0.wireOp",EDGE,"E0"),sQuery(id+"F0.wireOp",EDGE,"E1"),sQuery(id+"F0.wireOp",EDGE,"E2"),sQuery(id+"F0.wireOp",EDGE,"E3"),sQuery(id+"F0.wireOp",EDGE,"E4"),sQuery(id+"F0.wireOp",EDGE,"E5")])],"isStart":true});
            var sketch = newSketch(context, id + "F7", { "sketchPlane" : qUnion([Q0])});
            skLineSegment(sketch, "E17.bottom", {"start": v(-146.8, -466.79) * mm, "end": v(-334.75, -466.79) * mm});
            skLineSegment(sketch, "E17.top", {"start": v(-146.8, -222.44) * mm, "end": v(-334.75, -222.44) * mm});
            skLineSegment(sketch, "E17.left", {"start": v(-146.8, -466.79) * mm, "end": v(-146.8, -222.44) * mm});
            skLineSegment(sketch, "E17.right", {"start": v(-334.75, -466.79) * mm, "end": v(-334.75, -222.44) * mm});
            skLineSegment(sketch, "E18.bottom", {"start": v(-447.53, -335.22) * mm, "end": v(-353.55, -335.22) * mm});
            skLineSegment(sketch, "E18.top", {"start": v(-447.53, -410.4) * mm, "end": v(-353.55, -410.4) * mm});
            skLineSegment(sketch, "E18.left", {"start": v(-447.53, -335.22) * mm, "end": v(-447.53, -410.4) * mm});
            skLineSegment(sketch, "E18.right", {"start": v(-353.55, -335.22) * mm, "end": v(-353.55, -410.4) * mm});
            skLineSegment(sketch, "E19.bottom", {"start": v(-221.98, 266.26) * mm, "end": v(-128, 266.26) * mm});
            skLineSegment(sketch, "E19.top", {"start": v(-221.98, 191.07) * mm, "end": v(-128, 191.07) * mm});
            skLineSegment(sketch, "E19.left", {"start": v(-221.98, 266.26) * mm, "end": v(-221.98, 191.07) * mm});
            skLineSegment(sketch, "E19.right", {"start": v(-128, 266.26) * mm, "end": v(-128, 191.07) * mm});
            skLineSegment(sketch, "E20.bottom", {"start": v(-334.75, 266.26) * mm, "end": v(-240.77, 266.26) * mm});
            skLineSegment(sketch, "E20.top", {"start": v(-334.75, 191.07) * mm, "end": v(-240.77, 191.07) * mm});
            skLineSegment(sketch, "E20.left", {"start": v(-334.75, 266.26) * mm, "end": v(-334.75, 191.07) * mm});
            skLineSegment(sketch, "E20.right", {"start": v(-240.77, 266.26) * mm, "end": v(-240.77, 191.07) * mm});
            skLineSegment(sketch, "E21.bottom", {"start": v(-447.53, 266.26) * mm, "end": v(-353.55, 266.26) * mm});
            skLineSegment(sketch, "E21.top", {"start": v(-447.53, 191.07) * mm, "end": v(-353.55, 191.07) * mm});
            skLineSegment(sketch, "E21.left", {"start": v(-447.53, 266.26) * mm, "end": v(-447.53, 191.07) * mm});
            skLineSegment(sketch, "E21.right", {"start": v(-353.55, 266.26) * mm, "end": v(-353.55, 191.07) * mm});
            skLineSegment(sketch, "E22.bottom", {"start": v(-165.59, 172.28) * mm, "end": v(-128, 172.28) * mm});
            skLineSegment(sketch, "E22.top", {"start": v(-165.59, 134.68) * mm, "end": v(-128, 134.68) * mm});
            skLineSegment(sketch, "E22.left", {"start": v(-165.59, 172.28) * mm, "end": v(-165.59, 134.68) * mm});
            skLineSegment(sketch, "E22.right", {"start": v(-128, 172.28) * mm, "end": v(-128, 134.68) * mm});
            skLineSegment(sketch, "E23.0.1.0", {"start": v(-128, 115.89) * mm, "end": v(-128, 78.3) * mm});
            skLineSegment(sketch, "E23.0.1.1", {"start": v(-165.59, 78.3) * mm, "end": v(-128, 78.3) * mm});
            skLineSegment(sketch, "E23.0.1.2", {"start": v(-165.59, 115.89) * mm, "end": v(-165.59, 78.3) * mm});
            skLineSegment(sketch, "E23.0.1.3", {"start": v(-165.59, 115.89) * mm, "end": v(-128, 115.89) * mm});
            skLineSegment(sketch, "E23.0.2.0", {"start": v(-128, 59.5) * mm, "end": v(-128, 21.9) * mm});
            skLineSegment(sketch, "E23.0.2.1", {"start": v(-165.59, 21.9) * mm, "end": v(-128, 21.9) * mm});
            skLineSegment(sketch, "E23.0.2.2", {"start": v(-165.59, 59.5) * mm, "end": v(-165.59, 21.9) * mm});
            skLineSegment(sketch, "E23.0.2.3", {"start": v(-165.59, 59.5) * mm, "end": v(-128, 59.5) * mm});
            skLineSegment(sketch, "E23.0.3.0", {"start": v(-128, 3.11) * mm, "end": v(-128, -34.48) * mm});
            skLineSegment(sketch, "E23.0.3.1", {"start": v(-165.59, -34.48) * mm, "end": v(-128, -34.48) * mm});
            skLineSegment(sketch, "E23.0.3.2", {"start": v(-165.59, 3.11) * mm, "end": v(-165.59, -34.48) * mm});
            skLineSegment(sketch, "E23.0.3.3", {"start": v(-165.59, 3.11) * mm, "end": v(-128, 3.11) * mm});
            skLineSegment(sketch, "E23.0.4.0", {"start": v(-128, -53.28) * mm, "end": v(-128, -90.87) * mm});
            skLineSegment(sketch, "E23.0.4.1", {"start": v(-165.59, -90.87) * mm, "end": v(-128, -90.87) * mm});
            skLineSegment(sketch, "E23.0.4.2", {"start": v(-165.59, -53.28) * mm, "end": v(-165.59, -90.87) * mm});
            skLineSegment(sketch, "E23.0.4.3", {"start": v(-165.59, -53.28) * mm, "end": v(-128, -53.28) * mm});
            skLineSegment(sketch, "E23.0.5.0", {"start": v(-128, -109.66) * mm, "end": v(-128, -147.26) * mm});
            skLineSegment(sketch, "E23.0.5.1", {"start": v(-165.59, -147.26) * mm, "end": v(-128, -147.26) * mm});
            skLineSegment(sketch, "E23.0.5.2", {"start": v(-165.59, -109.66) * mm, "end": v(-165.59, -147.26) * mm});
            skLineSegment(sketch, "E23.0.5.3", {"start": v(-165.59, -109.66) * mm, "end": v(-128, -109.66) * mm});
            skLineSegment(sketch, "E23.0.6.0", {"start": v(-128, -166.05) * mm, "end": v(-128, -203.64) * mm});
            skLineSegment(sketch, "E23.0.6.1", {"start": v(-165.59, -203.64) * mm, "end": v(-128, -203.64) * mm});
            skLineSegment(sketch, "E23.0.6.2", {"start": v(-165.59, -166.05) * mm, "end": v(-165.59, -203.64) * mm});
            skLineSegment(sketch, "E23.0.6.3", {"start": v(-165.59, -166.05) * mm, "end": v(-128, -166.05) * mm});
            skLineSegment(sketch, "E23.1.0.0", {"start": v(-184.39, 172.28) * mm, "end": v(-184.39, 134.68) * mm});
            skLineSegment(sketch, "E23.1.0.1", {"start": v(-221.98, 134.68) * mm, "end": v(-184.39, 134.68) * mm});
            skLineSegment(sketch, "E23.1.0.2", {"start": v(-221.98, 172.28) * mm, "end": v(-221.98, 134.68) * mm});
            skLineSegment(sketch, "E23.1.0.3", {"start": v(-221.98, 172.28) * mm, "end": v(-184.39, 172.28) * mm});
            skLineSegment(sketch, "E23.1.1.0", {"start": v(-184.39, 115.89) * mm, "end": v(-184.39, 78.3) * mm});
            skLineSegment(sketch, "E23.1.1.1", {"start": v(-221.98, 78.3) * mm, "end": v(-184.39, 78.3) * mm});
            skLineSegment(sketch, "E23.1.1.2", {"start": v(-221.98, 115.89) * mm, "end": v(-221.98, 78.3) * mm});
            skLineSegment(sketch, "E23.1.1.3", {"start": v(-221.98, 115.89) * mm, "end": v(-184.39, 115.89) * mm});
            skLineSegment(sketch, "E23.1.2.0", {"start": v(-184.39, 59.5) * mm, "end": v(-184.39, 21.9) * mm});
            skLineSegment(sketch, "E23.1.2.1", {"start": v(-221.98, 21.9) * mm, "end": v(-184.39, 21.9) * mm});
            skLineSegment(sketch, "E23.1.2.2", {"start": v(-221.98, 59.5) * mm, "end": v(-221.98, 21.9) * mm});
            skLineSegment(sketch, "E23.1.2.3", {"start": v(-221.98, 59.5) * mm, "end": v(-184.39, 59.5) * mm});
            skLineSegment(sketch, "E23.1.3.0", {"start": v(-184.39, 3.11) * mm, "end": v(-184.39, -34.48) * mm});
            skLineSegment(sketch, "E23.1.3.1", {"start": v(-221.98, -34.48) * mm, "end": v(-184.39, -34.48) * mm});
            skLineSegment(sketch, "E23.1.3.2", {"start": v(-221.98, 3.11) * mm, "end": v(-221.98, -34.48) * mm});
            skLineSegment(sketch, "E23.1.3.3", {"start": v(-221.98, 3.11) * mm, "end": v(-184.39, 3.11) * mm});
            skLineSegment(sketch, "E23.1.4.0", {"start": v(-184.39, -53.28) * mm, "end": v(-184.39, -90.87) * mm});
            skLineSegment(sketch, "E23.1.4.1", {"start": v(-221.98, -90.87) * mm, "end": v(-184.39, -90.87) * mm});
            skLineSegment(sketch, "E23.1.4.2", {"start": v(-221.98, -53.28) * mm, "end": v(-221.98, -90.87) * mm});
            skLineSegment(sketch, "E23.1.4.3", {"start": v(-221.98, -53.28) * mm, "end": v(-184.39, -53.28) * mm});
            skLineSegment(sketch, "E23.1.5.0", {"start": v(-184.39, -109.66) * mm, "end": v(-184.39, -147.26) * mm});
            skLineSegment(sketch, "E23.1.5.1", {"start": v(-221.98, -147.26) * mm, "end": v(-184.39, -147.26) * mm});
            skLineSegment(sketch, "E23.1.5.2", {"start": v(-221.98, -109.66) * mm, "end": v(-221.98, -147.26) * mm});
            skLineSegment(sketch, "E23.1.5.3", {"start": v(-221.98, -109.66) * mm, "end": v(-184.39, -109.66) * mm});
            skLineSegment(sketch, "E23.1.6.0", {"start": v(-184.39, -166.05) * mm, "end": v(-184.39, -203.64) * mm});
            skLineSegment(sketch, "E23.1.6.1", {"start": v(-221.98, -203.64) * mm, "end": v(-184.39, -203.64) * mm});
            skLineSegment(sketch, "E23.1.6.2", {"start": v(-221.98, -166.05) * mm, "end": v(-221.98, -203.64) * mm});
            skLineSegment(sketch, "E23.1.6.3", {"start": v(-221.98, -166.05) * mm, "end": v(-184.39, -166.05) * mm});
            skLineSegment(sketch, "E23.2.0.0", {"start": v(-240.77, 172.28) * mm, "end": v(-240.77, 134.68) * mm});
            skLineSegment(sketch, "E23.2.0.1", {"start": v(-278.37, 134.68) * mm, "end": v(-240.77, 134.68) * mm});
            skLineSegment(sketch, "E23.2.0.2", {"start": v(-278.37, 172.28) * mm, "end": v(-278.37, 134.68) * mm});
            skLineSegment(sketch, "E23.2.0.3", {"start": v(-278.37, 172.28) * mm, "end": v(-240.77, 172.28) * mm});
            skLineSegment(sketch, "E23.2.1.0", {"start": v(-240.77, 115.89) * mm, "end": v(-240.77, 78.3) * mm});
            skLineSegment(sketch, "E23.2.1.1", {"start": v(-278.37, 78.3) * mm, "end": v(-240.77, 78.3) * mm});
            skLineSegment(sketch, "E23.2.1.2", {"start": v(-278.37, 115.89) * mm, "end": v(-278.37, 78.3) * mm});
            skLineSegment(sketch, "E23.2.1.3", {"start": v(-278.37, 115.89) * mm, "end": v(-240.77, 115.89) * mm});
            skLineSegment(sketch, "E23.2.2.0", {"start": v(-240.77, 59.5) * mm, "end": v(-240.77, 21.9) * mm});
            skLineSegment(sketch, "E23.2.2.1", {"start": v(-278.37, 21.9) * mm, "end": v(-240.77, 21.9) * mm});
            skLineSegment(sketch, "E23.2.2.2", {"start": v(-278.37, 59.5) * mm, "end": v(-278.37, 21.9) * mm});
            skLineSegment(sketch, "E23.2.2.3", {"start": v(-278.37, 59.5) * mm, "end": v(-240.77, 59.5) * mm});
            skLineSegment(sketch, "E23.2.3.0", {"start": v(-240.77, 3.11) * mm, "end": v(-240.77, -34.48) * mm});
            skLineSegment(sketch, "E23.2.3.1", {"start": v(-278.37, -34.48) * mm, "end": v(-240.77, -34.48) * mm});
            skLineSegment(sketch, "E23.2.3.2", {"start": v(-278.37, 3.11) * mm, "end": v(-278.37, -34.48) * mm});
            skLineSegment(sketch, "E23.2.3.3", {"start": v(-278.37, 3.11) * mm, "end": v(-240.77, 3.11) * mm});
            skLineSegment(sketch, "E23.2.4.0", {"start": v(-240.77, -53.28) * mm, "end": v(-240.77, -90.87) * mm});
            skLineSegment(sketch, "E23.2.4.1", {"start": v(-278.37, -90.87) * mm, "end": v(-240.77, -90.87) * mm});
            skLineSegment(sketch, "E23.2.4.2", {"start": v(-278.37, -53.28) * mm, "end": v(-278.37, -90.87) * mm});
            skLineSegment(sketch, "E23.2.4.3", {"start": v(-278.37, -53.28) * mm, "end": v(-240.77, -53.28) * mm});
            skLineSegment(sketch, "E23.2.5.0", {"start": v(-240.77, -109.66) * mm, "end": v(-240.77, -147.26) * mm});
            skLineSegment(sketch, "E23.2.5.1", {"start": v(-278.37, -147.26) * mm, "end": v(-240.77, -147.26) * mm});
            skLineSegment(sketch, "E23.2.5.2", {"start": v(-278.37, -109.66) * mm, "end": v(-278.37, -147.26) * mm});
            skLineSegment(sketch, "E23.2.5.3", {"start": v(-278.37, -109.66) * mm, "end": v(-240.77, -109.66) * mm});
            skLineSegment(sketch, "E23.2.6.0", {"start": v(-240.77, -166.05) * mm, "end": v(-240.77, -203.64) * mm});
            skLineSegment(sketch, "E23.2.6.1", {"start": v(-278.37, -203.64) * mm, "end": v(-240.77, -203.64) * mm});
            skLineSegment(sketch, "E23.2.6.2", {"start": v(-278.37, -166.05) * mm, "end": v(-278.37, -203.64) * mm});
            skLineSegment(sketch, "E23.2.6.3", {"start": v(-278.37, -166.05) * mm, "end": v(-240.77, -166.05) * mm});
            skLineSegment(sketch, "E23.3.0.0", {"start": v(-297.16, 172.28) * mm, "end": v(-297.16, 134.68) * mm});
            skLineSegment(sketch, "E23.3.0.1", {"start": v(-334.75, 134.68) * mm, "end": v(-297.16, 134.68) * mm});
            skLineSegment(sketch, "E23.3.0.2", {"start": v(-334.75, 172.28) * mm, "end": v(-334.75, 134.68) * mm});
            skLineSegment(sketch, "E23.3.0.3", {"start": v(-334.75, 172.28) * mm, "end": v(-297.16, 172.28) * mm});
            skLineSegment(sketch, "E23.3.1.0", {"start": v(-297.16, 115.89) * mm, "end": v(-297.16, 78.3) * mm});
            skLineSegment(sketch, "E23.3.1.1", {"start": v(-334.75, 78.3) * mm, "end": v(-297.16, 78.3) * mm});
            skLineSegment(sketch, "E23.3.1.2", {"start": v(-334.75, 115.89) * mm, "end": v(-334.75, 78.3) * mm});
            skLineSegment(sketch, "E23.3.1.3", {"start": v(-334.75, 115.89) * mm, "end": v(-297.16, 115.89) * mm});
            skLineSegment(sketch, "E23.3.2.0", {"start": v(-297.16, 59.5) * mm, "end": v(-297.16, 21.9) * mm});
            skLineSegment(sketch, "E23.3.2.1", {"start": v(-334.75, 21.9) * mm, "end": v(-297.16, 21.9) * mm});
            skLineSegment(sketch, "E23.3.2.2", {"start": v(-334.75, 59.5) * mm, "end": v(-334.75, 21.9) * mm});
            skLineSegment(sketch, "E23.3.2.3", {"start": v(-334.75, 59.5) * mm, "end": v(-297.16, 59.5) * mm});
            skLineSegment(sketch, "E23.3.3.0", {"start": v(-297.16, 3.11) * mm, "end": v(-297.16, -34.48) * mm});
            skLineSegment(sketch, "E23.3.3.1", {"start": v(-334.75, -34.48) * mm, "end": v(-297.16, -34.48) * mm});
            skLineSegment(sketch, "E23.3.3.2", {"start": v(-334.75, 3.11) * mm, "end": v(-334.75, -34.48) * mm});
            skLineSegment(sketch, "E23.3.3.3", {"start": v(-334.75, 3.11) * mm, "end": v(-297.16, 3.11) * mm});
            skLineSegment(sketch, "E23.3.4.0", {"start": v(-297.16, -53.28) * mm, "end": v(-297.16, -90.87) * mm});
            skLineSegment(sketch, "E23.3.4.1", {"start": v(-334.75, -90.87) * mm, "end": v(-297.16, -90.87) * mm});
            skLineSegment(sketch, "E23.3.4.2", {"start": v(-334.75, -53.28) * mm, "end": v(-334.75, -90.87) * mm});
            skLineSegment(sketch, "E23.3.4.3", {"start": v(-334.75, -53.28) * mm, "end": v(-297.16, -53.28) * mm});
            skLineSegment(sketch, "E23.3.5.0", {"start": v(-297.16, -109.66) * mm, "end": v(-297.16, -147.26) * mm});
            skLineSegment(sketch, "E23.3.5.1", {"start": v(-334.75, -147.26) * mm, "end": v(-297.16, -147.26) * mm});
            skLineSegment(sketch, "E23.3.5.2", {"start": v(-334.75, -109.66) * mm, "end": v(-334.75, -147.26) * mm});
            skLineSegment(sketch, "E23.3.5.3", {"start": v(-334.75, -109.66) * mm, "end": v(-297.16, -109.66) * mm});
            skLineSegment(sketch, "E23.3.6.0", {"start": v(-297.16, -166.05) * mm, "end": v(-297.16, -203.64) * mm});
            skLineSegment(sketch, "E23.3.6.1", {"start": v(-334.75, -203.64) * mm, "end": v(-297.16, -203.64) * mm});
            skLineSegment(sketch, "E23.3.6.2", {"start": v(-334.75, -166.05) * mm, "end": v(-334.75, -203.64) * mm});
            skLineSegment(sketch, "E23.3.6.3", {"start": v(-334.75, -166.05) * mm, "end": v(-297.16, -166.05) * mm});
            skLineSegment(sketch, "E23.4.0.0", {"start": v(-353.55, 172.28) * mm, "end": v(-353.55, 134.68) * mm});
            skLineSegment(sketch, "E23.4.0.1", {"start": v(-391.14, 134.68) * mm, "end": v(-353.55, 134.68) * mm});
            skLineSegment(sketch, "E23.4.0.2", {"start": v(-391.14, 172.28) * mm, "end": v(-391.14, 134.68) * mm});
            skLineSegment(sketch, "E23.4.0.3", {"start": v(-391.14, 172.28) * mm, "end": v(-353.55, 172.28) * mm});
            skLineSegment(sketch, "E23.4.1.0", {"start": v(-353.55, 115.89) * mm, "end": v(-353.55, 78.3) * mm});
            skLineSegment(sketch, "E23.4.1.1", {"start": v(-391.14, 78.3) * mm, "end": v(-353.55, 78.3) * mm});
            skLineSegment(sketch, "E23.4.1.2", {"start": v(-391.14, 115.89) * mm, "end": v(-391.14, 78.3) * mm});
            skLineSegment(sketch, "E23.4.1.3", {"start": v(-391.14, 115.89) * mm, "end": v(-353.55, 115.89) * mm});
            skLineSegment(sketch, "E23.4.2.0", {"start": v(-353.55, 59.5) * mm, "end": v(-353.55, 21.9) * mm});
            skLineSegment(sketch, "E23.4.2.1", {"start": v(-391.14, 21.9) * mm, "end": v(-353.55, 21.9) * mm});
            skLineSegment(sketch, "E23.4.2.2", {"start": v(-391.14, 59.5) * mm, "end": v(-391.14, 21.9) * mm});
            skLineSegment(sketch, "E23.4.2.3", {"start": v(-391.14, 59.5) * mm, "end": v(-353.55, 59.5) * mm});
            skLineSegment(sketch, "E23.4.3.0", {"start": v(-353.55, 3.11) * mm, "end": v(-353.55, -34.48) * mm});
            skLineSegment(sketch, "E23.4.3.1", {"start": v(-391.14, -34.48) * mm, "end": v(-353.55, -34.48) * mm});
            skLineSegment(sketch, "E23.4.3.2", {"start": v(-391.14, 3.11) * mm, "end": v(-391.14, -34.48) * mm});
            skLineSegment(sketch, "E23.4.3.3", {"start": v(-391.14, 3.11) * mm, "end": v(-353.55, 3.11) * mm});
            skLineSegment(sketch, "E23.4.4.0", {"start": v(-353.55, -53.28) * mm, "end": v(-353.55, -90.87) * mm});
            skLineSegment(sketch, "E23.4.4.1", {"start": v(-391.14, -90.87) * mm, "end": v(-353.55, -90.87) * mm});
            skLineSegment(sketch, "E23.4.4.2", {"start": v(-391.14, -53.28) * mm, "end": v(-391.14, -90.87) * mm});
            skLineSegment(sketch, "E23.4.4.3", {"start": v(-391.14, -53.28) * mm, "end": v(-353.55, -53.28) * mm});
            skLineSegment(sketch, "E23.4.5.0", {"start": v(-353.55, -109.66) * mm, "end": v(-353.55, -147.26) * mm});
            skLineSegment(sketch, "E23.4.5.1", {"start": v(-391.14, -147.26) * mm, "end": v(-353.55, -147.26) * mm});
            skLineSegment(sketch, "E23.4.5.2", {"start": v(-391.14, -109.66) * mm, "end": v(-391.14, -147.26) * mm});
            skLineSegment(sketch, "E23.4.5.3", {"start": v(-391.14, -109.66) * mm, "end": v(-353.55, -109.66) * mm});
            skLineSegment(sketch, "E23.4.6.0", {"start": v(-353.55, -166.05) * mm, "end": v(-353.55, -203.64) * mm});
            skLineSegment(sketch, "E23.4.6.1", {"start": v(-391.14, -203.64) * mm, "end": v(-353.55, -203.64) * mm});
            skLineSegment(sketch, "E23.4.6.2", {"start": v(-391.14, -166.05) * mm, "end": v(-391.14, -203.64) * mm});
            skLineSegment(sketch, "E23.4.6.3", {"start": v(-391.14, -166.05) * mm, "end": v(-353.55, -166.05) * mm});
            skLineSegment(sketch, "E23.4.7.0", {"start": v(-353.55, -222.44) * mm, "end": v(-353.55, -260.03) * mm});
            skLineSegment(sketch, "E23.4.7.1", {"start": v(-391.14, -260.03) * mm, "end": v(-353.55, -260.03) * mm});
            skLineSegment(sketch, "E23.4.7.2", {"start": v(-391.14, -222.44) * mm, "end": v(-391.14, -260.03) * mm});
            skLineSegment(sketch, "E23.4.7.3", {"start": v(-391.14, -222.44) * mm, "end": v(-353.55, -222.44) * mm});
            skLineSegment(sketch, "E23.4.8.0", {"start": v(-353.55, -278.83) * mm, "end": v(-353.55, -316.42) * mm});
            skLineSegment(sketch, "E23.4.8.1", {"start": v(-391.14, -316.42) * mm, "end": v(-353.55, -316.42) * mm});
            skLineSegment(sketch, "E23.4.8.2", {"start": v(-391.14, -278.83) * mm, "end": v(-391.14, -316.42) * mm});
            skLineSegment(sketch, "E23.4.8.3", {"start": v(-391.14, -278.83) * mm, "end": v(-353.55, -278.83) * mm});
            skLineSegment(sketch, "E23.5.0.0", {"start": v(-409.94, 172.28) * mm, "end": v(-409.94, 134.68) * mm});
            skLineSegment(sketch, "E23.5.0.1", {"start": v(-447.53, 134.68) * mm, "end": v(-409.94, 134.68) * mm});
            skLineSegment(sketch, "E23.5.0.2", {"start": v(-447.53, 172.28) * mm, "end": v(-447.53, 134.68) * mm});
            skLineSegment(sketch, "E23.5.0.3", {"start": v(-447.53, 172.28) * mm, "end": v(-409.94, 172.28) * mm});
            skLineSegment(sketch, "E23.5.1.0", {"start": v(-409.94, 115.89) * mm, "end": v(-409.94, 78.3) * mm});
            skLineSegment(sketch, "E23.5.1.1", {"start": v(-447.53, 78.3) * mm, "end": v(-409.94, 78.3) * mm});
            skLineSegment(sketch, "E23.5.1.2", {"start": v(-447.53, 115.89) * mm, "end": v(-447.53, 78.3) * mm});
            skLineSegment(sketch, "E23.5.1.3", {"start": v(-447.53, 115.89) * mm, "end": v(-409.94, 115.89) * mm});
            skLineSegment(sketch, "E23.5.2.0", {"start": v(-409.94, 59.5) * mm, "end": v(-409.94, 21.9) * mm});
            skLineSegment(sketch, "E23.5.2.1", {"start": v(-447.53, 21.9) * mm, "end": v(-409.94, 21.9) * mm});
            skLineSegment(sketch, "E23.5.2.2", {"start": v(-447.53, 59.5) * mm, "end": v(-447.53, 21.9) * mm});
            skLineSegment(sketch, "E23.5.2.3", {"start": v(-447.53, 59.5) * mm, "end": v(-409.94, 59.5) * mm});
            skLineSegment(sketch, "E23.5.3.0", {"start": v(-409.94, 3.11) * mm, "end": v(-409.94, -34.48) * mm});
            skLineSegment(sketch, "E23.5.3.1", {"start": v(-447.53, -34.48) * mm, "end": v(-409.94, -34.48) * mm});
            skLineSegment(sketch, "E23.5.3.2", {"start": v(-447.53, 3.11) * mm, "end": v(-447.53, -34.48) * mm});
            skLineSegment(sketch, "E23.5.3.3", {"start": v(-447.53, 3.11) * mm, "end": v(-409.94, 3.11) * mm});
            skLineSegment(sketch, "E23.5.4.0", {"start": v(-409.94, -53.28) * mm, "end": v(-409.94, -90.87) * mm});
            skLineSegment(sketch, "E23.5.4.1", {"start": v(-447.53, -90.87) * mm, "end": v(-409.94, -90.87) * mm});
            skLineSegment(sketch, "E23.5.4.2", {"start": v(-447.53, -53.28) * mm, "end": v(-447.53, -90.87) * mm});
            skLineSegment(sketch, "E23.5.4.3", {"start": v(-447.53, -53.28) * mm, "end": v(-409.94, -53.28) * mm});
            skLineSegment(sketch, "E23.5.5.0", {"start": v(-409.94, -109.66) * mm, "end": v(-409.94, -147.26) * mm});
            skLineSegment(sketch, "E23.5.5.1", {"start": v(-447.53, -147.26) * mm, "end": v(-409.94, -147.26) * mm});
            skLineSegment(sketch, "E23.5.5.2", {"start": v(-447.53, -109.66) * mm, "end": v(-447.53, -147.26) * mm});
            skLineSegment(sketch, "E23.5.5.3", {"start": v(-447.53, -109.66) * mm, "end": v(-409.94, -109.66) * mm});
            skLineSegment(sketch, "E23.5.6.0", {"start": v(-409.94, -166.05) * mm, "end": v(-409.94, -203.64) * mm});
            skLineSegment(sketch, "E23.5.6.1", {"start": v(-447.53, -203.64) * mm, "end": v(-409.94, -203.64) * mm});
            skLineSegment(sketch, "E23.5.6.2", {"start": v(-447.53, -166.05) * mm, "end": v(-447.53, -203.64) * mm});
            skLineSegment(sketch, "E23.5.6.3", {"start": v(-447.53, -166.05) * mm, "end": v(-409.94, -166.05) * mm});
            skLineSegment(sketch, "E23.5.7.0", {"start": v(-409.94, -222.44) * mm, "end": v(-409.94, -260.03) * mm});
            skLineSegment(sketch, "E23.5.7.1", {"start": v(-447.53, -260.03) * mm, "end": v(-409.94, -260.03) * mm});
            skLineSegment(sketch, "E23.5.7.2", {"start": v(-447.53, -222.44) * mm, "end": v(-447.53, -260.03) * mm});
            skLineSegment(sketch, "E23.5.7.3", {"start": v(-447.53, -222.44) * mm, "end": v(-409.94, -222.44) * mm});
            skLineSegment(sketch, "E23.5.8.0", {"start": v(-409.94, -278.83) * mm, "end": v(-409.94, -316.42) * mm});
            skLineSegment(sketch, "E23.5.8.1", {"start": v(-447.53, -316.42) * mm, "end": v(-409.94, -316.42) * mm});
            skLineSegment(sketch, "E23.5.8.2", {"start": v(-447.53, -278.83) * mm, "end": v(-447.53, -316.42) * mm});
            skLineSegment(sketch, "E23.5.8.3", {"start": v(-447.53, -278.83) * mm, "end": v(-409.94, -278.83) * mm});
            skLineSegment(sketch, "E23.direction1", {"start": v(-165.59, 134.68) * mm, "end": v(-221.98, 134.68) * mm, "construction": true});
            skLineSegment(sketch, "E23.direction2", {"start": v(-165.59, 134.68) * mm, "end": v(-165.59, 78.3) * mm, "construction": true});
            skLineSegment(sketch, "E24.direction1", {"start": v(-447.53, -278.83) * mm, "end": v(-503.92, -278.83) * mm, "construction": true});
            skLineSegment(sketch, "E24.direction2", {"start": v(-447.53, -278.83) * mm, "end": v(-447.53, -222.44) * mm, "construction": true});
            skSolve(sketch);
        }
        {
            var Q0;
            Q0=makeQuery(id+"F7.imprint","IMPRINT",FACE,{"disambiguationData":[TD([[makeQuery(id+"F7.imprint","IMPRINT",EDGE,{"derivedFrom":sQuery(id+"F7.wireOp",EDGE,"E21.bottom")}),-1.0]])]});
            var Q1;
            Q1=makeQuery(id+"F7.imprint","IMPRINT",FACE,{"disambiguationData":[TD([[makeQuery(id+"F7.imprint","IMPRINT",EDGE,{"derivedFrom":sQuery(id+"F7.wireOp",EDGE,"E20.bottom")}),-1.0]])]});
            var Q2;
            Q2=makeQuery(id+"F7.imprint","IMPRINT",FACE,{"disambiguationData":[TD([[makeQuery(id+"F7.imprint","IMPRINT",EDGE,{"derivedFrom":sQuery(id+"F7.wireOp",EDGE,"E19.bottom")}),-1.0]])]});
            var Q3;
            Q3=makeQuery(id+"F7.imprint","IMPRINT",FACE,{"disambiguationData":[TD([[makeQuery(id+"F7.imprint","IMPRINT",EDGE,{"derivedFrom":sQuery(id+"F7.wireOp",EDGE,"E18.bottom")}),-1.0]])]});
            extrude(context, id + "F8", {"entities" : qUnion([Q0, Q1, Q2, Q3]), "operationType" : NewBodyOperationType.REMOVE, "oppositeDirection" : true, "depth" : 19.05 * mm});
        }
        {
            var Q0;
            Q0 = qSketchRegion(id + "F7", true);
            extrude(context, id + "F9", {"entities" : qUnion([Q0]), "operationType" : NewBodyOperationType.REMOVE, "oppositeDirection" : true, "depth" : 6.35 * mm});
        }
        {
            var Q0;
            Q0=makeQuery(id+"F1.opExtrude","SWEPT_FACE",FACE,{"disambiguationData":[OSD([sQuery(id+"F0.wireOp",EDGE,"E1")])]});
            var sketch = newSketch(context, id + "F10", { "sketchPlane" : qUnion([Q0])});
            skLineSegment(sketch, "E25.bottom", {"start": v(-451.1, -278.83) * mm, "end": v(-413.51, -278.83) * mm});
            skLineSegment(sketch, "E25.top", {"start": v(-451.1, -316.42) * mm, "end": v(-413.51, -316.42) * mm});
            skLineSegment(sketch, "E25.left", {"start": v(-451.1, -278.83) * mm, "end": v(-451.1, -316.42) * mm});
            skLineSegment(sketch, "E25.right", {"start": v(-413.51, -278.83) * mm, "end": v(-413.51, -316.42) * mm});
            skLineSegment(sketch, "E26.0.1.0", {"start": v(-451.1, -222.44) * mm, "end": v(-413.51, -222.44) * mm});
            skLineSegment(sketch, "E26.0.1.1", {"start": v(-451.1, -260.03) * mm, "end": v(-413.51, -260.03) * mm});
            skLineSegment(sketch, "E26.0.1.2", {"start": v(-451.1, -222.44) * mm, "end": v(-451.1, -260.03) * mm});
            skLineSegment(sketch, "E26.0.1.3", {"start": v(-413.51, -222.44) * mm, "end": v(-413.51, -260.03) * mm});
            skLineSegment(sketch, "E26.0.2.0", {"start": v(-451.1, -166.05) * mm, "end": v(-413.51, -166.05) * mm});
            skLineSegment(sketch, "E26.0.2.1", {"start": v(-451.1, -203.64) * mm, "end": v(-413.51, -203.64) * mm});
            skLineSegment(sketch, "E26.0.2.2", {"start": v(-451.1, -166.05) * mm, "end": v(-451.1, -203.64) * mm});
            skLineSegment(sketch, "E26.0.2.3", {"start": v(-413.51, -166.05) * mm, "end": v(-413.51, -203.64) * mm});
            skLineSegment(sketch, "E26.0.3.0", {"start": v(-451.1, -109.66) * mm, "end": v(-413.51, -109.66) * mm});
            skLineSegment(sketch, "E26.0.3.1", {"start": v(-451.1, -147.26) * mm, "end": v(-413.51, -147.26) * mm});
            skLineSegment(sketch, "E26.0.3.2", {"start": v(-451.1, -109.66) * mm, "end": v(-451.1, -147.26) * mm});
            skLineSegment(sketch, "E26.0.3.3", {"start": v(-413.51, -109.66) * mm, "end": v(-413.51, -147.26) * mm});
            skLineSegment(sketch, "E26.0.4.0", {"start": v(-451.1, -53.28) * mm, "end": v(-413.51, -53.28) * mm});
            skLineSegment(sketch, "E26.0.4.1", {"start": v(-451.1, -90.87) * mm, "end": v(-413.51, -90.87) * mm});
            skLineSegment(sketch, "E26.0.4.2", {"start": v(-451.1, -53.28) * mm, "end": v(-451.1, -90.87) * mm});
            skLineSegment(sketch, "E26.0.4.3", {"start": v(-413.51, -53.28) * mm, "end": v(-413.51, -90.87) * mm});
            skLineSegment(sketch, "E26.0.5.0", {"start": v(-451.1, 3.11) * mm, "end": v(-413.51, 3.11) * mm});
            skLineSegment(sketch, "E26.0.5.1", {"start": v(-451.1, -34.48) * mm, "end": v(-413.51, -34.48) * mm});
            skLineSegment(sketch, "E26.0.5.2", {"start": v(-451.1, 3.11) * mm, "end": v(-451.1, -34.48) * mm});
            skLineSegment(sketch, "E26.0.5.3", {"start": v(-413.51, 3.11) * mm, "end": v(-413.51, -34.48) * mm});
            skLineSegment(sketch, "E26.0.6.0", {"start": v(-451.1, 59.5) * mm, "end": v(-413.51, 59.5) * mm});
            skLineSegment(sketch, "E26.0.6.1", {"start": v(-451.1, 21.9) * mm, "end": v(-413.51, 21.9) * mm});
            skLineSegment(sketch, "E26.0.6.2", {"start": v(-451.1, 59.5) * mm, "end": v(-451.1, 21.9) * mm});
            skLineSegment(sketch, "E26.0.6.3", {"start": v(-413.51, 59.5) * mm, "end": v(-413.51, 21.9) * mm});
            skLineSegment(sketch, "E26.0.7.0", {"start": v(-451.1, 115.89) * mm, "end": v(-413.51, 115.89) * mm});
            skLineSegment(sketch, "E26.0.7.1", {"start": v(-451.1, 78.3) * mm, "end": v(-413.51, 78.3) * mm});
            skLineSegment(sketch, "E26.0.7.2", {"start": v(-451.1, 115.89) * mm, "end": v(-451.1, 78.3) * mm});
            skLineSegment(sketch, "E26.0.7.3", {"start": v(-413.51, 115.89) * mm, "end": v(-413.51, 78.3) * mm});
            skLineSegment(sketch, "E26.0.8.0", {"start": v(-451.1, 172.28) * mm, "end": v(-413.51, 172.28) * mm});
            skLineSegment(sketch, "E26.0.8.1", {"start": v(-451.1, 134.68) * mm, "end": v(-413.51, 134.68) * mm});
            skLineSegment(sketch, "E26.0.8.2", {"start": v(-451.1, 172.28) * mm, "end": v(-451.1, 134.68) * mm});
            skLineSegment(sketch, "E26.0.8.3", {"start": v(-413.51, 172.28) * mm, "end": v(-413.51, 134.68) * mm});
            skLineSegment(sketch, "E26.1.0.0", {"start": v(-394.72, -278.83) * mm, "end": v(-357.12, -278.83) * mm});
            skLineSegment(sketch, "E26.1.0.1", {"start": v(-394.72, -316.42) * mm, "end": v(-357.12, -316.42) * mm});
            skLineSegment(sketch, "E26.1.0.2", {"start": v(-394.72, -278.83) * mm, "end": v(-394.72, -316.42) * mm});
            skLineSegment(sketch, "E26.1.0.3", {"start": v(-357.12, -278.83) * mm, "end": v(-357.12, -316.42) * mm});
            skLineSegment(sketch, "E26.1.1.0", {"start": v(-394.72, -222.44) * mm, "end": v(-357.12, -222.44) * mm});
            skLineSegment(sketch, "E26.1.1.1", {"start": v(-394.72, -260.03) * mm, "end": v(-357.12, -260.03) * mm});
            skLineSegment(sketch, "E26.1.1.2", {"start": v(-394.72, -222.44) * mm, "end": v(-394.72, -260.03) * mm});
            skLineSegment(sketch, "E26.1.1.3", {"start": v(-357.12, -222.44) * mm, "end": v(-357.12, -260.03) * mm});
            skLineSegment(sketch, "E26.1.2.0", {"start": v(-394.72, -166.05) * mm, "end": v(-357.12, -166.05) * mm});
            skLineSegment(sketch, "E26.1.2.1", {"start": v(-394.72, -203.64) * mm, "end": v(-357.12, -203.64) * mm});
            skLineSegment(sketch, "E26.1.2.2", {"start": v(-394.72, -166.05) * mm, "end": v(-394.72, -203.64) * mm});
            skLineSegment(sketch, "E26.1.2.3", {"start": v(-357.12, -166.05) * mm, "end": v(-357.12, -203.64) * mm});
            skLineSegment(sketch, "E26.1.3.0", {"start": v(-394.72, -109.66) * mm, "end": v(-357.12, -109.66) * mm});
            skLineSegment(sketch, "E26.1.3.1", {"start": v(-394.72, -147.26) * mm, "end": v(-357.12, -147.26) * mm});
            skLineSegment(sketch, "E26.1.3.2", {"start": v(-394.72, -109.66) * mm, "end": v(-394.72, -147.26) * mm});
            skLineSegment(sketch, "E26.1.3.3", {"start": v(-357.12, -109.66) * mm, "end": v(-357.12, -147.26) * mm});
            skLineSegment(sketch, "E26.1.4.0", {"start": v(-394.72, -53.28) * mm, "end": v(-357.12, -53.28) * mm});
            skLineSegment(sketch, "E26.1.4.1", {"start": v(-394.72, -90.87) * mm, "end": v(-357.12, -90.87) * mm});
            skLineSegment(sketch, "E26.1.4.2", {"start": v(-394.72, -53.28) * mm, "end": v(-394.72, -90.87) * mm});
            skLineSegment(sketch, "E26.1.4.3", {"start": v(-357.12, -53.28) * mm, "end": v(-357.12, -90.87) * mm});
            skLineSegment(sketch, "E26.1.5.0", {"start": v(-394.72, 3.11) * mm, "end": v(-357.12, 3.11) * mm});
            skLineSegment(sketch, "E26.1.5.1", {"start": v(-394.72, -34.48) * mm, "end": v(-357.12, -34.48) * mm});
            skLineSegment(sketch, "E26.1.5.2", {"start": v(-394.72, 3.11) * mm, "end": v(-394.72, -34.48) * mm});
            skLineSegment(sketch, "E26.1.5.3", {"start": v(-357.12, 3.11) * mm, "end": v(-357.12, -34.48) * mm});
            skLineSegment(sketch, "E26.1.6.0", {"start": v(-394.72, 59.5) * mm, "end": v(-357.12, 59.5) * mm});
            skLineSegment(sketch, "E26.1.6.1", {"start": v(-394.72, 21.9) * mm, "end": v(-357.12, 21.9) * mm});
            skLineSegment(sketch, "E26.1.6.2", {"start": v(-394.72, 59.5) * mm, "end": v(-394.72, 21.9) * mm});
            skLineSegment(sketch, "E26.1.6.3", {"start": v(-357.12, 59.5) * mm, "end": v(-357.12, 21.9) * mm});
            skLineSegment(sketch, "E26.1.7.0", {"start": v(-394.72, 115.89) * mm, "end": v(-357.12, 115.89) * mm});
            skLineSegment(sketch, "E26.1.7.1", {"start": v(-394.72, 78.3) * mm, "end": v(-357.12, 78.3) * mm});
            skLineSegment(sketch, "E26.1.7.2", {"start": v(-394.72, 115.89) * mm, "end": v(-394.72, 78.3) * mm});
            skLineSegment(sketch, "E26.1.7.3", {"start": v(-357.12, 115.89) * mm, "end": v(-357.12, 78.3) * mm});
            skLineSegment(sketch, "E26.1.8.0", {"start": v(-394.72, 172.28) * mm, "end": v(-357.12, 172.28) * mm});
            skLineSegment(sketch, "E26.1.8.1", {"start": v(-394.72, 134.68) * mm, "end": v(-357.12, 134.68) * mm});
            skLineSegment(sketch, "E26.1.8.2", {"start": v(-394.72, 172.28) * mm, "end": v(-394.72, 134.68) * mm});
            skLineSegment(sketch, "E26.1.8.3", {"start": v(-357.12, 172.28) * mm, "end": v(-357.12, 134.68) * mm});
            skLineSegment(sketch, "E26.2.0.0", {"start": v(-338.33, -278.83) * mm, "end": v(-300.74, -278.83) * mm});
            skLineSegment(sketch, "E26.2.0.1", {"start": v(-338.33, -316.42) * mm, "end": v(-300.74, -316.42) * mm});
            skLineSegment(sketch, "E26.2.0.2", {"start": v(-338.33, -278.83) * mm, "end": v(-338.33, -316.42) * mm});
            skLineSegment(sketch, "E26.2.0.3", {"start": v(-300.74, -278.83) * mm, "end": v(-300.74, -316.42) * mm});
            skLineSegment(sketch, "E26.2.1.0", {"start": v(-338.33, -222.44) * mm, "end": v(-300.74, -222.44) * mm});
            skLineSegment(sketch, "E26.2.1.1", {"start": v(-338.33, -260.03) * mm, "end": v(-300.74, -260.03) * mm});
            skLineSegment(sketch, "E26.2.1.2", {"start": v(-338.33, -222.44) * mm, "end": v(-338.33, -260.03) * mm});
            skLineSegment(sketch, "E26.2.1.3", {"start": v(-300.74, -222.44) * mm, "end": v(-300.74, -260.03) * mm});
            skLineSegment(sketch, "E26.2.2.0", {"start": v(-338.33, -166.05) * mm, "end": v(-300.74, -166.05) * mm});
            skLineSegment(sketch, "E26.2.2.1", {"start": v(-338.33, -203.64) * mm, "end": v(-300.74, -203.64) * mm});
            skLineSegment(sketch, "E26.2.2.2", {"start": v(-338.33, -166.05) * mm, "end": v(-338.33, -203.64) * mm});
            skLineSegment(sketch, "E26.2.2.3", {"start": v(-300.74, -166.05) * mm, "end": v(-300.74, -203.64) * mm});
            skLineSegment(sketch, "E26.2.3.0", {"start": v(-338.33, -109.66) * mm, "end": v(-300.74, -109.66) * mm});
            skLineSegment(sketch, "E26.2.3.1", {"start": v(-338.33, -147.26) * mm, "end": v(-300.74, -147.26) * mm});
            skLineSegment(sketch, "E26.2.3.2", {"start": v(-338.33, -109.66) * mm, "end": v(-338.33, -147.26) * mm});
            skLineSegment(sketch, "E26.2.3.3", {"start": v(-300.74, -109.66) * mm, "end": v(-300.74, -147.26) * mm});
            skLineSegment(sketch, "E26.2.4.0", {"start": v(-338.33, -53.28) * mm, "end": v(-300.74, -53.28) * mm});
            skLineSegment(sketch, "E26.2.4.1", {"start": v(-338.33, -90.87) * mm, "end": v(-300.74, -90.87) * mm});
            skLineSegment(sketch, "E26.2.4.2", {"start": v(-338.33, -53.28) * mm, "end": v(-338.33, -90.87) * mm});
            skLineSegment(sketch, "E26.2.4.3", {"start": v(-300.74, -53.28) * mm, "end": v(-300.74, -90.87) * mm});
            skLineSegment(sketch, "E26.2.5.0", {"start": v(-338.33, 3.11) * mm, "end": v(-300.74, 3.11) * mm});
            skLineSegment(sketch, "E26.2.5.1", {"start": v(-338.33, -34.48) * mm, "end": v(-300.74, -34.48) * mm});
            skLineSegment(sketch, "E26.2.5.2", {"start": v(-338.33, 3.11) * mm, "end": v(-338.33, -34.48) * mm});
            skLineSegment(sketch, "E26.2.5.3", {"start": v(-300.74, 3.11) * mm, "end": v(-300.74, -34.48) * mm});
            skLineSegment(sketch, "E26.2.6.0", {"start": v(-338.33, 59.5) * mm, "end": v(-300.74, 59.5) * mm});
            skLineSegment(sketch, "E26.2.6.1", {"start": v(-338.33, 21.9) * mm, "end": v(-300.74, 21.9) * mm});
            skLineSegment(sketch, "E26.2.6.2", {"start": v(-338.33, 59.5) * mm, "end": v(-338.33, 21.9) * mm});
            skLineSegment(sketch, "E26.2.6.3", {"start": v(-300.74, 59.5) * mm, "end": v(-300.74, 21.9) * mm});
            skLineSegment(sketch, "E26.2.7.0", {"start": v(-338.33, 115.89) * mm, "end": v(-300.74, 115.89) * mm});
            skLineSegment(sketch, "E26.2.7.1", {"start": v(-338.33, 78.3) * mm, "end": v(-300.74, 78.3) * mm});
            skLineSegment(sketch, "E26.2.7.2", {"start": v(-338.33, 115.89) * mm, "end": v(-338.33, 78.3) * mm});
            skLineSegment(sketch, "E26.2.7.3", {"start": v(-300.74, 115.89) * mm, "end": v(-300.74, 78.3) * mm});
            skLineSegment(sketch, "E26.2.8.0", {"start": v(-338.33, 172.28) * mm, "end": v(-300.74, 172.28) * mm});
            skLineSegment(sketch, "E26.2.8.1", {"start": v(-338.33, 134.68) * mm, "end": v(-300.74, 134.68) * mm});
            skLineSegment(sketch, "E26.2.8.2", {"start": v(-338.33, 172.28) * mm, "end": v(-338.33, 134.68) * mm});
            skLineSegment(sketch, "E26.2.8.3", {"start": v(-300.74, 172.28) * mm, "end": v(-300.74, 134.68) * mm});
            skLineSegment(sketch, "E26.direction1", {"start": v(-451.1, -278.83) * mm, "end": v(-394.72, -278.83) * mm, "construction": true});
            skLineSegment(sketch, "E26.direction2", {"start": v(-451.1, -278.83) * mm, "end": v(-451.1, -222.44) * mm, "construction": true});
            skLineSegment(sketch, "E27.0.3.0", {"start": v(-281.94, -278.83) * mm, "end": v(-244.35, -278.83) * mm});
            skLineSegment(sketch, "E27.3.3.0", {"start": v(-281.94, -316.42) * mm, "end": v(-244.35, -316.42) * mm});
            skLineSegment(sketch, "E27.6.3.0", {"start": v(-281.94, -278.83) * mm, "end": v(-281.94, -316.42) * mm});
            skLineSegment(sketch, "E27.9.3.0", {"start": v(-244.35, -278.83) * mm, "end": v(-244.35, -316.42) * mm});
            skLineSegment(sketch, "E27.0.3.1", {"start": v(-281.94, -222.44) * mm, "end": v(-244.35, -222.44) * mm});
            skLineSegment(sketch, "E27.3.3.1", {"start": v(-281.94, -260.03) * mm, "end": v(-244.35, -260.03) * mm});
            skLineSegment(sketch, "E27.6.3.1", {"start": v(-281.94, -222.44) * mm, "end": v(-281.94, -260.03) * mm});
            skLineSegment(sketch, "E27.9.3.1", {"start": v(-244.35, -222.44) * mm, "end": v(-244.35, -260.03) * mm});
            skLineSegment(sketch, "E27.0.3.2", {"start": v(-281.94, -166.05) * mm, "end": v(-244.35, -166.05) * mm});
            skLineSegment(sketch, "E27.3.3.2", {"start": v(-281.94, -203.64) * mm, "end": v(-244.35, -203.64) * mm});
            skLineSegment(sketch, "E27.6.3.2", {"start": v(-281.94, -166.05) * mm, "end": v(-281.94, -203.64) * mm});
            skLineSegment(sketch, "E27.9.3.2", {"start": v(-244.35, -166.05) * mm, "end": v(-244.35, -203.64) * mm});
            skLineSegment(sketch, "E27.0.3.3", {"start": v(-281.94, -109.66) * mm, "end": v(-244.35, -109.66) * mm});
            skLineSegment(sketch, "E27.3.3.3", {"start": v(-281.94, -147.26) * mm, "end": v(-244.35, -147.26) * mm});
            skLineSegment(sketch, "E27.6.3.3", {"start": v(-281.94, -109.66) * mm, "end": v(-281.94, -147.26) * mm});
            skLineSegment(sketch, "E27.9.3.3", {"start": v(-244.35, -109.66) * mm, "end": v(-244.35, -147.26) * mm});
            skLineSegment(sketch, "E27.0.3.4", {"start": v(-281.94, -53.28) * mm, "end": v(-244.35, -53.28) * mm});
            skLineSegment(sketch, "E27.3.3.4", {"start": v(-281.94, -90.87) * mm, "end": v(-244.35, -90.87) * mm});
            skLineSegment(sketch, "E27.6.3.4", {"start": v(-281.94, -53.28) * mm, "end": v(-281.94, -90.87) * mm});
            skLineSegment(sketch, "E27.9.3.4", {"start": v(-244.35, -53.28) * mm, "end": v(-244.35, -90.87) * mm});
            skLineSegment(sketch, "E27.0.3.5", {"start": v(-281.94, 3.11) * mm, "end": v(-244.35, 3.11) * mm});
            skLineSegment(sketch, "E27.3.3.5", {"start": v(-281.94, -34.48) * mm, "end": v(-244.35, -34.48) * mm});
            skLineSegment(sketch, "E27.6.3.5", {"start": v(-281.94, 3.11) * mm, "end": v(-281.94, -34.48) * mm});
            skLineSegment(sketch, "E27.9.3.5", {"start": v(-244.35, 3.11) * mm, "end": v(-244.35, -34.48) * mm});
            skLineSegment(sketch, "E27.0.3.6", {"start": v(-281.94, 59.5) * mm, "end": v(-244.35, 59.5) * mm});
            skLineSegment(sketch, "E27.3.3.6", {"start": v(-281.94, 21.9) * mm, "end": v(-244.35, 21.9) * mm});
            skLineSegment(sketch, "E27.6.3.6", {"start": v(-281.94, 59.5) * mm, "end": v(-281.94, 21.9) * mm});
            skLineSegment(sketch, "E27.9.3.6", {"start": v(-244.35, 59.5) * mm, "end": v(-244.35, 21.9) * mm});
            skLineSegment(sketch, "E27.0.3.7", {"start": v(-281.94, 115.89) * mm, "end": v(-244.35, 115.89) * mm});
            skLineSegment(sketch, "E27.3.3.7", {"start": v(-281.94, 78.3) * mm, "end": v(-244.35, 78.3) * mm});
            skLineSegment(sketch, "E27.6.3.7", {"start": v(-281.94, 115.89) * mm, "end": v(-281.94, 78.3) * mm});
            skLineSegment(sketch, "E27.9.3.7", {"start": v(-244.35, 115.89) * mm, "end": v(-244.35, 78.3) * mm});
            skLineSegment(sketch, "E27.0.3.8", {"start": v(-281.94, 172.28) * mm, "end": v(-244.35, 172.28) * mm});
            skLineSegment(sketch, "E27.3.3.8", {"start": v(-281.94, 134.68) * mm, "end": v(-244.35, 134.68) * mm});
            skLineSegment(sketch, "E27.6.3.8", {"start": v(-281.94, 172.28) * mm, "end": v(-281.94, 134.68) * mm});
            skLineSegment(sketch, "E27.9.3.8", {"start": v(-244.35, 172.28) * mm, "end": v(-244.35, 134.68) * mm});
            skLineSegment(sketch, "E28.0.2.0", {"start": v(-338.33, 266.26) * mm, "end": v(-244.35, 266.26) * mm});
            skLineSegment(sketch, "E28.3.2.0", {"start": v(-338.33, 191.07) * mm, "end": v(-244.35, 191.07) * mm});
            skLineSegment(sketch, "E28.9.2.0", {"start": v(-338.33, 266.26) * mm, "end": v(-338.33, 191.07) * mm});
            skLineSegment(sketch, "E28.0.3.0", {"start": v(-451.1, 266.26) * mm, "end": v(-357.12, 266.26) * mm});
            skLineSegment(sketch, "E28.3.3.0", {"start": v(-451.1, 191.07) * mm, "end": v(-357.12, 191.07) * mm});
            skLineSegment(sketch, "E28.6.3.0", {"start": v(-357.12, 266.26) * mm, "end": v(-357.12, 191.07) * mm});
            skLineSegment(sketch, "E28.9.3.0", {"start": v(-451.1, 266.26) * mm, "end": v(-451.1, 191.07) * mm});
            skLineSegment(sketch, "E29", {"start": v(-244.35, 266.26) * mm, "end": v(-244.35, 191.07) * mm});
            skLineSegment(sketch, "E30.bottom", {"start": v(-451.1, -335.22) * mm, "end": v(-357.12, -335.22) * mm});
            skLineSegment(sketch, "E30.top", {"start": v(-451.1, -410.4) * mm, "end": v(-357.12, -410.4) * mm});
            skLineSegment(sketch, "E30.left", {"start": v(-451.1, -335.22) * mm, "end": v(-451.1, -410.4) * mm});
            skLineSegment(sketch, "E30.right", {"start": v(-357.12, -335.22) * mm, "end": v(-357.12, -410.4) * mm});
            skLineSegment(sketch, "E31.bottom", {"start": v(-338.33, -335.22) * mm, "end": v(-244.35, -335.22) * mm});
            skLineSegment(sketch, "E31.top", {"start": v(-338.33, -410.4) * mm, "end": v(-244.35, -410.4) * mm});
            skLineSegment(sketch, "E31.left", {"start": v(-338.33, -335.22) * mm, "end": v(-338.33, -410.4) * mm});
            skLineSegment(sketch, "E31.right", {"start": v(-244.35, -335.22) * mm, "end": v(-244.35, -410.4) * mm});
            skSolve(sketch);
        }
        {
            var Q0;
            Q0=makeQuery(id+"F10.imprint","IMPRINT",FACE,{"disambiguationData":[TD([[makeQuery(id+"F10.imprint","IMPRINT",EDGE,{"derivedFrom":sQuery(id+"F10.wireOp",EDGE,"E31.bottom")}),-1.0]])]});
            var Q1;
            Q1=makeQuery(id+"F10.imprint","IMPRINT",FACE,{"disambiguationData":[TD([[makeQuery(id+"F10.imprint","IMPRINT",EDGE,{"derivedFrom":sQuery(id+"F10.wireOp",EDGE,"E30.bottom")}),-1.0]])]});
            var Q2;
            Q2=makeQuery(id+"F10.imprint","IMPRINT",FACE,{"disambiguationData":[TD([[makeQuery(id+"F10.imprint","IMPRINT",EDGE,{"derivedFrom":sQuery(id+"F10.wireOp",EDGE,"E28.0.3.0")}),-1.0]])]});
            var Q3;
            Q3=makeQuery(id+"F10.imprint","IMPRINT",FACE,{"disambiguationData":[TD([[makeQuery(id+"F10.imprint","IMPRINT",EDGE,{"derivedFrom":sQuery(id+"F10.wireOp",EDGE,"E28.0.2.0")}),-1.0]])]});
            extrude(context, id + "F11", {"entities" : qUnion([Q0, Q1, Q2, Q3]), "operationType" : NewBodyOperationType.REMOVE, "oppositeDirection" : true, "depth" : 19.05 * mm});
        }
        {
            var Q0;
            Q0 = qSketchRegion(id + "F10", true);
            extrude(context, id + "F12", {"entities" : qUnion([Q0]), "operationType" : NewBodyOperationType.REMOVE, "oppositeDirection" : true, "depth" : 6.35 * mm});
        }
        {
            var Q0;
            {var subQ0=sQuery(id+"F0.wireOp",EDGE,"E5");Q0=makeQuery(id+"FeAJW4w09d5ZraR_2.opBoolean","MERGE",FACE,{"derivedFrom":[makeQuery(id+"F1.opExtrude","SWEPT_FACE",FACE,{"disambiguationData":[OSD([subQ0])]}),makeQuery(id+"F3.opExtrude","SWEPT_FACE",FACE,{"disambiguationData":[OSD([sQuery(id+"F0.wireOp",EDGE,"E4"),subQ0])]})]});}
            var sketch = newSketch(context, id + "F13", { "sketchPlane" : qUnion([Q0])});
            skLineSegment(sketch, "E32.bottom", {"start": v(18.8, 266.26) * mm, "end": v(112.78, 266.26) * mm});
            skLineSegment(sketch, "E32.top", {"start": v(18.8, 191.07) * mm, "end": v(112.78, 191.07) * mm});
            skLineSegment(sketch, "E32.left", {"start": v(18.8, 266.26) * mm, "end": v(18.8, 191.07) * mm});
            skLineSegment(sketch, "E32.right", {"start": v(112.78, 266.26) * mm, "end": v(112.78, 191.07) * mm});
            skLineSegment(sketch, "E33.1.0.0", {"start": v(131.57, 266.26) * mm, "end": v(225.55, 266.26) * mm});
            skLineSegment(sketch, "E33.1.0.1", {"start": v(131.57, 191.07) * mm, "end": v(225.55, 191.07) * mm});
            skLineSegment(sketch, "E33.1.0.2", {"start": v(225.55, 266.26) * mm, "end": v(225.55, 191.07) * mm});
            skLineSegment(sketch, "E33.1.0.3", {"start": v(131.57, 266.26) * mm, "end": v(131.57, 191.07) * mm});
            skLineSegment(sketch, "E33.direction1", {"start": v(18.8, 266.26) * mm, "end": v(131.57, 266.26) * mm, "construction": true});
            skPoint(sketch, "E34.0", {"position": v(18.8, 172.28) * mm});
            skPoint(sketch, "E35.0", {"position": v(56.39, 172.28) * mm});
            skPoint(sketch, "E36.0", {"position": v(56.39, 134.68) * mm});
            skPoint(sketch, "E37.0", {"position": v(18.8, 134.68) * mm});
            skLineSegment(sketch, "E38", {"start": v(18.8, 172.28) * mm, "end": v(18.8, 134.68) * mm});
            skLineSegment(sketch, "E39", {"start": v(56.39, 134.68) * mm, "end": v(56.39, 172.28) * mm});
            skLineSegment(sketch, "E40", {"start": v(56.39, 172.28) * mm, "end": v(18.8, 172.28) * mm});
            skLineSegment(sketch, "E41", {"start": v(18.8, 134.68) * mm, "end": v(56.39, 134.68) * mm});
            skLineSegment(sketch, "E42.0.1.0", {"start": v(56.39, 115.89) * mm, "end": v(18.8, 115.89) * mm});
            skLineSegment(sketch, "E42.0.1.1", {"start": v(18.8, 78.3) * mm, "end": v(56.39, 78.3) * mm});
            skLineSegment(sketch, "E42.0.1.2", {"start": v(56.39, 78.3) * mm, "end": v(56.39, 115.89) * mm});
            skLineSegment(sketch, "E42.0.1.3", {"start": v(18.8, 115.89) * mm, "end": v(18.8, 78.3) * mm});
            skLineSegment(sketch, "E42.0.2.0", {"start": v(56.39, 59.5) * mm, "end": v(18.8, 59.5) * mm});
            skLineSegment(sketch, "E42.0.2.1", {"start": v(18.8, 21.9) * mm, "end": v(56.39, 21.9) * mm});
            skLineSegment(sketch, "E42.0.2.2", {"start": v(56.39, 21.9) * mm, "end": v(56.39, 59.5) * mm});
            skLineSegment(sketch, "E42.0.2.3", {"start": v(18.8, 59.5) * mm, "end": v(18.8, 21.9) * mm});
            skLineSegment(sketch, "E42.0.3.0", {"start": v(56.39, 3.11) * mm, "end": v(18.8, 3.11) * mm});
            skLineSegment(sketch, "E42.0.3.1", {"start": v(18.8, -34.48) * mm, "end": v(56.39, -34.48) * mm});
            skLineSegment(sketch, "E42.0.3.2", {"start": v(56.39, -34.48) * mm, "end": v(56.39, 3.11) * mm});
            skLineSegment(sketch, "E42.0.3.3", {"start": v(18.8, 3.11) * mm, "end": v(18.8, -34.48) * mm});
            skLineSegment(sketch, "E42.0.4.0", {"start": v(56.39, -53.28) * mm, "end": v(18.8, -53.28) * mm});
            skLineSegment(sketch, "E42.0.4.1", {"start": v(18.8, -90.87) * mm, "end": v(56.39, -90.87) * mm});
            skLineSegment(sketch, "E42.0.4.2", {"start": v(56.39, -90.87) * mm, "end": v(56.39, -53.28) * mm});
            skLineSegment(sketch, "E42.0.4.3", {"start": v(18.8, -53.28) * mm, "end": v(18.8, -90.87) * mm});
            skLineSegment(sketch, "E42.0.5.0", {"start": v(56.39, -109.66) * mm, "end": v(18.8, -109.66) * mm});
            skLineSegment(sketch, "E42.0.5.1", {"start": v(18.8, -147.26) * mm, "end": v(56.39, -147.26) * mm});
            skLineSegment(sketch, "E42.0.5.2", {"start": v(56.39, -147.26) * mm, "end": v(56.39, -109.66) * mm});
            skLineSegment(sketch, "E42.0.5.3", {"start": v(18.8, -109.66) * mm, "end": v(18.8, -147.26) * mm});
            skLineSegment(sketch, "E42.0.6.0", {"start": v(56.39, -166.05) * mm, "end": v(18.8, -166.05) * mm});
            skLineSegment(sketch, "E42.0.6.1", {"start": v(18.8, -203.64) * mm, "end": v(56.39, -203.64) * mm});
            skLineSegment(sketch, "E42.0.6.2", {"start": v(56.39, -203.64) * mm, "end": v(56.39, -166.05) * mm});
            skLineSegment(sketch, "E42.0.6.3", {"start": v(18.8, -166.05) * mm, "end": v(18.8, -203.64) * mm});
            skLineSegment(sketch, "E42.1.0.0", {"start": v(112.78, 172.28) * mm, "end": v(75.18, 172.28) * mm});
            skLineSegment(sketch, "E42.1.0.1", {"start": v(75.18, 134.68) * mm, "end": v(112.78, 134.68) * mm});
            skLineSegment(sketch, "E42.1.0.2", {"start": v(112.78, 134.68) * mm, "end": v(112.78, 172.28) * mm});
            skLineSegment(sketch, "E42.1.0.3", {"start": v(75.18, 172.28) * mm, "end": v(75.18, 134.68) * mm});
            skLineSegment(sketch, "E42.1.1.0", {"start": v(112.78, 115.89) * mm, "end": v(75.18, 115.89) * mm});
            skLineSegment(sketch, "E42.1.1.1", {"start": v(75.18, 78.3) * mm, "end": v(112.78, 78.3) * mm});
            skLineSegment(sketch, "E42.1.1.2", {"start": v(112.78, 78.3) * mm, "end": v(112.78, 115.89) * mm});
            skLineSegment(sketch, "E42.1.1.3", {"start": v(75.18, 115.89) * mm, "end": v(75.18, 78.3) * mm});
            skLineSegment(sketch, "E42.1.2.0", {"start": v(112.78, 59.5) * mm, "end": v(75.18, 59.5) * mm});
            skLineSegment(sketch, "E42.1.2.1", {"start": v(75.18, 21.9) * mm, "end": v(112.78, 21.9) * mm});
            skLineSegment(sketch, "E42.1.2.2", {"start": v(112.78, 21.9) * mm, "end": v(112.78, 59.5) * mm});
            skLineSegment(sketch, "E42.1.2.3", {"start": v(75.18, 59.5) * mm, "end": v(75.18, 21.9) * mm});
            skLineSegment(sketch, "E42.1.3.0", {"start": v(112.78, 3.11) * mm, "end": v(75.18, 3.11) * mm});
            skLineSegment(sketch, "E42.1.3.1", {"start": v(75.18, -34.48) * mm, "end": v(112.78, -34.48) * mm});
            skLineSegment(sketch, "E42.1.3.2", {"start": v(112.78, -34.48) * mm, "end": v(112.78, 3.11) * mm});
            skLineSegment(sketch, "E42.1.3.3", {"start": v(75.18, 3.11) * mm, "end": v(75.18, -34.48) * mm});
            skLineSegment(sketch, "E42.1.4.0", {"start": v(112.78, -53.28) * mm, "end": v(75.18, -53.28) * mm});
            skLineSegment(sketch, "E42.1.4.1", {"start": v(75.18, -90.87) * mm, "end": v(112.78, -90.87) * mm});
            skLineSegment(sketch, "E42.1.4.2", {"start": v(112.78, -90.87) * mm, "end": v(112.78, -53.28) * mm});
            skLineSegment(sketch, "E42.1.4.3", {"start": v(75.18, -53.28) * mm, "end": v(75.18, -90.87) * mm});
            skLineSegment(sketch, "E42.1.5.0", {"start": v(112.78, -109.66) * mm, "end": v(75.18, -109.66) * mm});
            skLineSegment(sketch, "E42.1.5.1", {"start": v(75.18, -147.26) * mm, "end": v(112.78, -147.26) * mm});
            skLineSegment(sketch, "E42.1.5.2", {"start": v(112.78, -147.26) * mm, "end": v(112.78, -109.66) * mm});
            skLineSegment(sketch, "E42.1.5.3", {"start": v(75.18, -109.66) * mm, "end": v(75.18, -147.26) * mm});
            skLineSegment(sketch, "E42.1.6.0", {"start": v(112.78, -166.05) * mm, "end": v(75.18, -166.05) * mm});
            skLineSegment(sketch, "E42.1.6.1", {"start": v(75.18, -203.64) * mm, "end": v(112.78, -203.64) * mm});
            skLineSegment(sketch, "E42.1.6.2", {"start": v(112.78, -203.64) * mm, "end": v(112.78, -166.05) * mm});
            skLineSegment(sketch, "E42.1.6.3", {"start": v(75.18, -166.05) * mm, "end": v(75.18, -203.64) * mm});
            skLineSegment(sketch, "E42.2.0.0", {"start": v(169.16, 172.28) * mm, "end": v(131.57, 172.28) * mm});
            skLineSegment(sketch, "E42.2.0.1", {"start": v(131.57, 134.68) * mm, "end": v(169.16, 134.68) * mm});
            skLineSegment(sketch, "E42.2.0.2", {"start": v(169.16, 134.68) * mm, "end": v(169.16, 172.28) * mm});
            skLineSegment(sketch, "E42.2.0.3", {"start": v(131.57, 172.28) * mm, "end": v(131.57, 134.68) * mm});
            skLineSegment(sketch, "E42.2.1.0", {"start": v(169.16, 115.89) * mm, "end": v(131.57, 115.89) * mm});
            skLineSegment(sketch, "E42.2.1.1", {"start": v(131.57, 78.3) * mm, "end": v(169.16, 78.3) * mm});
            skLineSegment(sketch, "E42.2.1.2", {"start": v(169.16, 78.3) * mm, "end": v(169.16, 115.89) * mm});
            skLineSegment(sketch, "E42.2.1.3", {"start": v(131.57, 115.89) * mm, "end": v(131.57, 78.3) * mm});
            skLineSegment(sketch, "E42.2.2.0", {"start": v(169.16, 59.5) * mm, "end": v(131.57, 59.5) * mm});
            skLineSegment(sketch, "E42.2.2.1", {"start": v(131.57, 21.9) * mm, "end": v(169.16, 21.9) * mm});
            skLineSegment(sketch, "E42.2.2.2", {"start": v(169.16, 21.9) * mm, "end": v(169.16, 59.5) * mm});
            skLineSegment(sketch, "E42.2.2.3", {"start": v(131.57, 59.5) * mm, "end": v(131.57, 21.9) * mm});
            skLineSegment(sketch, "E42.2.3.0", {"start": v(169.16, 3.11) * mm, "end": v(131.57, 3.11) * mm});
            skLineSegment(sketch, "E42.2.3.1", {"start": v(131.57, -34.48) * mm, "end": v(169.16, -34.48) * mm});
            skLineSegment(sketch, "E42.2.3.2", {"start": v(169.16, -34.48) * mm, "end": v(169.16, 3.11) * mm});
            skLineSegment(sketch, "E42.2.3.3", {"start": v(131.57, 3.11) * mm, "end": v(131.57, -34.48) * mm});
            skLineSegment(sketch, "E42.2.4.0", {"start": v(169.16, -53.28) * mm, "end": v(131.57, -53.28) * mm});
            skLineSegment(sketch, "E42.2.4.1", {"start": v(131.57, -90.87) * mm, "end": v(169.16, -90.87) * mm});
            skLineSegment(sketch, "E42.2.4.2", {"start": v(169.16, -90.87) * mm, "end": v(169.16, -53.28) * mm});
            skLineSegment(sketch, "E42.2.4.3", {"start": v(131.57, -53.28) * mm, "end": v(131.57, -90.87) * mm});
            skLineSegment(sketch, "E42.2.5.0", {"start": v(169.16, -109.66) * mm, "end": v(131.57, -109.66) * mm});
            skLineSegment(sketch, "E42.2.5.1", {"start": v(131.57, -147.26) * mm, "end": v(169.16, -147.26) * mm});
            skLineSegment(sketch, "E42.2.5.2", {"start": v(169.16, -147.26) * mm, "end": v(169.16, -109.66) * mm});
            skLineSegment(sketch, "E42.2.5.3", {"start": v(131.57, -109.66) * mm, "end": v(131.57, -147.26) * mm});
            skLineSegment(sketch, "E42.2.6.0", {"start": v(169.16, -166.05) * mm, "end": v(131.57, -166.05) * mm});
            skLineSegment(sketch, "E42.2.6.1", {"start": v(131.57, -203.64) * mm, "end": v(169.16, -203.64) * mm});
            skLineSegment(sketch, "E42.2.6.2", {"start": v(169.16, -203.64) * mm, "end": v(169.16, -166.05) * mm});
            skLineSegment(sketch, "E42.2.6.3", {"start": v(131.57, -166.05) * mm, "end": v(131.57, -203.64) * mm});
            skLineSegment(sketch, "E42.3.0.0", {"start": v(225.55, 172.28) * mm, "end": v(187.96, 172.28) * mm});
            skLineSegment(sketch, "E42.3.0.1", {"start": v(187.96, 134.68) * mm, "end": v(225.55, 134.68) * mm});
            skLineSegment(sketch, "E42.3.0.2", {"start": v(225.55, 134.68) * mm, "end": v(225.55, 172.28) * mm});
            skLineSegment(sketch, "E42.3.0.3", {"start": v(187.96, 172.28) * mm, "end": v(187.96, 134.68) * mm});
            skLineSegment(sketch, "E42.3.1.0", {"start": v(225.55, 115.89) * mm, "end": v(187.96, 115.89) * mm});
            skLineSegment(sketch, "E42.3.1.1", {"start": v(187.96, 78.3) * mm, "end": v(225.55, 78.3) * mm});
            skLineSegment(sketch, "E42.3.1.2", {"start": v(225.55, 78.3) * mm, "end": v(225.55, 115.89) * mm});
            skLineSegment(sketch, "E42.3.1.3", {"start": v(187.96, 115.89) * mm, "end": v(187.96, 78.3) * mm});
            skLineSegment(sketch, "E42.3.2.0", {"start": v(225.55, 59.5) * mm, "end": v(187.96, 59.5) * mm});
            skLineSegment(sketch, "E42.3.2.1", {"start": v(187.96, 21.9) * mm, "end": v(225.55, 21.9) * mm});
            skLineSegment(sketch, "E42.3.2.2", {"start": v(225.55, 21.9) * mm, "end": v(225.55, 59.5) * mm});
            skLineSegment(sketch, "E42.3.2.3", {"start": v(187.96, 59.5) * mm, "end": v(187.96, 21.9) * mm});
            skLineSegment(sketch, "E42.3.3.0", {"start": v(225.55, 3.11) * mm, "end": v(187.96, 3.11) * mm});
            skLineSegment(sketch, "E42.3.3.1", {"start": v(187.96, -34.48) * mm, "end": v(225.55, -34.48) * mm});
            skLineSegment(sketch, "E42.3.3.2", {"start": v(225.55, -34.48) * mm, "end": v(225.55, 3.11) * mm});
            skLineSegment(sketch, "E42.3.3.3", {"start": v(187.96, 3.11) * mm, "end": v(187.96, -34.48) * mm});
            skLineSegment(sketch, "E42.3.4.0", {"start": v(225.55, -53.28) * mm, "end": v(187.96, -53.28) * mm});
            skLineSegment(sketch, "E42.3.4.1", {"start": v(187.96, -90.87) * mm, "end": v(225.55, -90.87) * mm});
            skLineSegment(sketch, "E42.3.4.2", {"start": v(225.55, -90.87) * mm, "end": v(225.55, -53.28) * mm});
            skLineSegment(sketch, "E42.3.4.3", {"start": v(187.96, -53.28) * mm, "end": v(187.96, -90.87) * mm});
            skLineSegment(sketch, "E42.3.5.0", {"start": v(225.55, -109.66) * mm, "end": v(187.96, -109.66) * mm});
            skLineSegment(sketch, "E42.3.5.1", {"start": v(187.96, -147.26) * mm, "end": v(225.55, -147.26) * mm});
            skLineSegment(sketch, "E42.3.5.2", {"start": v(225.55, -147.26) * mm, "end": v(225.55, -109.66) * mm});
            skLineSegment(sketch, "E42.3.5.3", {"start": v(187.96, -109.66) * mm, "end": v(187.96, -147.26) * mm});
            skLineSegment(sketch, "E42.3.6.0", {"start": v(225.55, -166.05) * mm, "end": v(187.96, -166.05) * mm});
            skLineSegment(sketch, "E42.3.6.1", {"start": v(187.96, -203.64) * mm, "end": v(225.55, -203.64) * mm});
            skLineSegment(sketch, "E42.3.6.2", {"start": v(225.55, -203.64) * mm, "end": v(225.55, -166.05) * mm});
            skLineSegment(sketch, "E42.3.6.3", {"start": v(187.96, -166.05) * mm, "end": v(187.96, -203.64) * mm});
            skLineSegment(sketch, "E42.4.3.0", {"start": v(281.94, 3.11) * mm, "end": v(244.35, 3.11) * mm});
            skLineSegment(sketch, "E42.4.3.1", {"start": v(244.35, -34.48) * mm, "end": v(281.94, -34.48) * mm});
            skLineSegment(sketch, "E42.4.3.2", {"start": v(281.94, -34.48) * mm, "end": v(281.94, 3.11) * mm});
            skLineSegment(sketch, "E42.4.3.3", {"start": v(244.35, 3.11) * mm, "end": v(244.35, -34.48) * mm});
            skLineSegment(sketch, "E42.4.4.0", {"start": v(281.94, -53.28) * mm, "end": v(244.35, -53.28) * mm});
            skLineSegment(sketch, "E42.4.4.1", {"start": v(244.35, -90.87) * mm, "end": v(281.94, -90.87) * mm});
            skLineSegment(sketch, "E42.4.4.2", {"start": v(281.94, -90.87) * mm, "end": v(281.94, -53.28) * mm});
            skLineSegment(sketch, "E42.4.4.3", {"start": v(244.35, -53.28) * mm, "end": v(244.35, -90.87) * mm});
            skLineSegment(sketch, "E42.4.5.0", {"start": v(281.94, -109.66) * mm, "end": v(244.35, -109.66) * mm});
            skLineSegment(sketch, "E42.4.5.1", {"start": v(244.35, -147.26) * mm, "end": v(281.94, -147.26) * mm});
            skLineSegment(sketch, "E42.4.5.2", {"start": v(281.94, -147.26) * mm, "end": v(281.94, -109.66) * mm});
            skLineSegment(sketch, "E42.4.5.3", {"start": v(244.35, -109.66) * mm, "end": v(244.35, -147.26) * mm});
            skLineSegment(sketch, "E42.4.6.0", {"start": v(281.94, -166.05) * mm, "end": v(244.35, -166.05) * mm});
            skLineSegment(sketch, "E42.4.6.1", {"start": v(244.35, -203.64) * mm, "end": v(281.94, -203.64) * mm});
            skLineSegment(sketch, "E42.4.6.2", {"start": v(281.94, -203.64) * mm, "end": v(281.94, -166.05) * mm});
            skLineSegment(sketch, "E42.4.6.3", {"start": v(244.35, -166.05) * mm, "end": v(244.35, -203.64) * mm});
            skLineSegment(sketch, "E42.4.7.0", {"start": v(281.94, -222.44) * mm, "end": v(244.35, -222.44) * mm});
            skLineSegment(sketch, "E42.4.7.1", {"start": v(244.35, -260.03) * mm, "end": v(281.94, -260.03) * mm});
            skLineSegment(sketch, "E42.4.7.2", {"start": v(281.94, -260.03) * mm, "end": v(281.94, -222.44) * mm});
            skLineSegment(sketch, "E42.4.7.3", {"start": v(244.35, -222.44) * mm, "end": v(244.35, -260.03) * mm});
            skLineSegment(sketch, "E42.5.3.0", {"start": v(338.33, 3.11) * mm, "end": v(300.74, 3.11) * mm});
            skLineSegment(sketch, "E42.5.3.1", {"start": v(300.74, -34.48) * mm, "end": v(338.33, -34.48) * mm});
            skLineSegment(sketch, "E42.5.3.2", {"start": v(338.33, -34.48) * mm, "end": v(338.33, 3.11) * mm});
            skLineSegment(sketch, "E42.5.3.3", {"start": v(300.74, 3.11) * mm, "end": v(300.74, -34.48) * mm});
            skLineSegment(sketch, "E42.5.4.0", {"start": v(338.33, -53.28) * mm, "end": v(300.74, -53.28) * mm});
            skLineSegment(sketch, "E42.5.4.1", {"start": v(300.74, -90.87) * mm, "end": v(338.33, -90.87) * mm});
            skLineSegment(sketch, "E42.5.4.2", {"start": v(338.33, -90.87) * mm, "end": v(338.33, -53.28) * mm});
            skLineSegment(sketch, "E42.5.4.3", {"start": v(300.74, -53.28) * mm, "end": v(300.74, -90.87) * mm});
            skLineSegment(sketch, "E42.5.5.0", {"start": v(338.33, -109.66) * mm, "end": v(300.74, -109.66) * mm});
            skLineSegment(sketch, "E42.5.5.1", {"start": v(300.74, -147.26) * mm, "end": v(338.33, -147.26) * mm});
            skLineSegment(sketch, "E42.5.5.2", {"start": v(338.33, -147.26) * mm, "end": v(338.33, -109.66) * mm});
            skLineSegment(sketch, "E42.5.5.3", {"start": v(300.74, -109.66) * mm, "end": v(300.74, -147.26) * mm});
            skLineSegment(sketch, "E42.5.6.0", {"start": v(338.33, -166.05) * mm, "end": v(300.74, -166.05) * mm});
            skLineSegment(sketch, "E42.5.6.1", {"start": v(300.74, -203.64) * mm, "end": v(338.33, -203.64) * mm});
            skLineSegment(sketch, "E42.5.6.2", {"start": v(338.33, -203.64) * mm, "end": v(338.33, -166.05) * mm});
            skLineSegment(sketch, "E42.5.6.3", {"start": v(300.74, -166.05) * mm, "end": v(300.74, -203.64) * mm});
            skLineSegment(sketch, "E42.5.7.0", {"start": v(338.33, -222.44) * mm, "end": v(300.74, -222.44) * mm});
            skLineSegment(sketch, "E42.5.7.1", {"start": v(300.74, -260.03) * mm, "end": v(338.33, -260.03) * mm});
            skLineSegment(sketch, "E42.5.7.2", {"start": v(338.33, -260.03) * mm, "end": v(338.33, -222.44) * mm});
            skLineSegment(sketch, "E42.5.7.3", {"start": v(300.74, -222.44) * mm, "end": v(300.74, -260.03) * mm});
            skLineSegment(sketch, "E42.6.3.0", {"start": v(394.72, 3.11) * mm, "end": v(357.12, 3.11) * mm});
            skLineSegment(sketch, "E42.6.3.1", {"start": v(357.12, -34.48) * mm, "end": v(394.72, -34.48) * mm});
            skLineSegment(sketch, "E42.6.3.2", {"start": v(394.72, -34.48) * mm, "end": v(394.72, 3.11) * mm});
            skLineSegment(sketch, "E42.6.3.3", {"start": v(357.12, 3.11) * mm, "end": v(357.12, -34.48) * mm});
            skLineSegment(sketch, "E42.6.4.0", {"start": v(394.72, -53.28) * mm, "end": v(357.12, -53.28) * mm});
            skLineSegment(sketch, "E42.6.4.1", {"start": v(357.12, -90.87) * mm, "end": v(394.72, -90.87) * mm});
            skLineSegment(sketch, "E42.6.4.2", {"start": v(394.72, -90.87) * mm, "end": v(394.72, -53.28) * mm});
            skLineSegment(sketch, "E42.6.4.3", {"start": v(357.12, -53.28) * mm, "end": v(357.12, -90.87) * mm});
            skLineSegment(sketch, "E42.6.5.0", {"start": v(394.72, -109.66) * mm, "end": v(357.12, -109.66) * mm});
            skLineSegment(sketch, "E42.6.5.1", {"start": v(357.12, -147.26) * mm, "end": v(394.72, -147.26) * mm});
            skLineSegment(sketch, "E42.6.5.2", {"start": v(394.72, -147.26) * mm, "end": v(394.72, -109.66) * mm});
            skLineSegment(sketch, "E42.6.5.3", {"start": v(357.12, -109.66) * mm, "end": v(357.12, -147.26) * mm});
            skLineSegment(sketch, "E42.6.6.0", {"start": v(394.72, -166.05) * mm, "end": v(357.12, -166.05) * mm});
            skLineSegment(sketch, "E42.6.6.1", {"start": v(357.12, -203.64) * mm, "end": v(394.72, -203.64) * mm});
            skLineSegment(sketch, "E42.6.6.2", {"start": v(394.72, -203.64) * mm, "end": v(394.72, -166.05) * mm});
            skLineSegment(sketch, "E42.6.6.3", {"start": v(357.12, -166.05) * mm, "end": v(357.12, -203.64) * mm});
            skLineSegment(sketch, "E42.6.7.0", {"start": v(394.72, -222.44) * mm, "end": v(357.12, -222.44) * mm});
            skLineSegment(sketch, "E42.6.7.1", {"start": v(357.12, -260.03) * mm, "end": v(394.72, -260.03) * mm});
            skLineSegment(sketch, "E42.6.7.2", {"start": v(394.72, -260.03) * mm, "end": v(394.72, -222.44) * mm});
            skLineSegment(sketch, "E42.6.7.3", {"start": v(357.12, -222.44) * mm, "end": v(357.12, -260.03) * mm});
            skLineSegment(sketch, "E42.7.3.0", {"start": v(451.1, 3.11) * mm, "end": v(413.51, 3.11) * mm});
            skLineSegment(sketch, "E42.7.3.1", {"start": v(413.51, -34.48) * mm, "end": v(451.1, -34.48) * mm});
            skLineSegment(sketch, "E42.7.3.2", {"start": v(451.1, -34.48) * mm, "end": v(451.1, 3.11) * mm});
            skLineSegment(sketch, "E42.7.3.3", {"start": v(413.51, 3.11) * mm, "end": v(413.51, -34.48) * mm});
            skLineSegment(sketch, "E42.7.4.0", {"start": v(451.1, -53.28) * mm, "end": v(413.51, -53.28) * mm});
            skLineSegment(sketch, "E42.7.4.1", {"start": v(413.51, -90.87) * mm, "end": v(451.1, -90.87) * mm});
            skLineSegment(sketch, "E42.7.4.2", {"start": v(451.1, -90.87) * mm, "end": v(451.1, -53.28) * mm});
            skLineSegment(sketch, "E42.7.4.3", {"start": v(413.51, -53.28) * mm, "end": v(413.51, -90.87) * mm});
            skLineSegment(sketch, "E42.7.5.0", {"start": v(451.1, -109.66) * mm, "end": v(413.51, -109.66) * mm});
            skLineSegment(sketch, "E42.7.5.1", {"start": v(413.51, -147.26) * mm, "end": v(451.1, -147.26) * mm});
            skLineSegment(sketch, "E42.7.5.2", {"start": v(451.1, -147.26) * mm, "end": v(451.1, -109.66) * mm});
            skLineSegment(sketch, "E42.7.5.3", {"start": v(413.51, -109.66) * mm, "end": v(413.51, -147.26) * mm});
            skLineSegment(sketch, "E42.7.6.0", {"start": v(451.1, -166.05) * mm, "end": v(413.51, -166.05) * mm});
            skLineSegment(sketch, "E42.7.6.1", {"start": v(413.51, -203.64) * mm, "end": v(451.1, -203.64) * mm});
            skLineSegment(sketch, "E42.7.6.2", {"start": v(451.1, -203.64) * mm, "end": v(451.1, -166.05) * mm});
            skLineSegment(sketch, "E42.7.6.3", {"start": v(413.51, -166.05) * mm, "end": v(413.51, -203.64) * mm});
            skLineSegment(sketch, "E42.7.7.0", {"start": v(451.1, -222.44) * mm, "end": v(413.51, -222.44) * mm});
            skLineSegment(sketch, "E42.7.7.1", {"start": v(413.51, -260.03) * mm, "end": v(451.1, -260.03) * mm});
            skLineSegment(sketch, "E42.7.7.2", {"start": v(451.1, -260.03) * mm, "end": v(451.1, -222.44) * mm});
            skLineSegment(sketch, "E42.7.7.3", {"start": v(413.51, -222.44) * mm, "end": v(413.51, -260.03) * mm});
            skLineSegment(sketch, "E42.direction1", {"start": v(18.8, 134.68) * mm, "end": v(75.18, 134.68) * mm, "construction": true});
            skLineSegment(sketch, "E42.direction2", {"start": v(18.8, 134.68) * mm, "end": v(18.8, 78.3) * mm, "construction": true});
            skLineSegment(sketch, "E43.0.4.8", {"start": v(281.94, -278.83) * mm, "end": v(244.35, -278.83) * mm});
            skLineSegment(sketch, "E43.3.4.8", {"start": v(244.35, -316.42) * mm, "end": v(281.94, -316.42) * mm});
            skLineSegment(sketch, "E43.6.4.8", {"start": v(281.94, -316.42) * mm, "end": v(281.94, -278.83) * mm});
            skLineSegment(sketch, "E43.9.4.8", {"start": v(244.35, -278.83) * mm, "end": v(244.35, -316.42) * mm});
            skLineSegment(sketch, "E43.0.5.8", {"start": v(338.33, -278.83) * mm, "end": v(300.74, -278.83) * mm});
            skLineSegment(sketch, "E43.3.5.8", {"start": v(300.74, -316.42) * mm, "end": v(338.33, -316.42) * mm});
            skLineSegment(sketch, "E43.6.5.8", {"start": v(338.33, -316.42) * mm, "end": v(338.33, -278.83) * mm});
            skLineSegment(sketch, "E43.9.5.8", {"start": v(300.74, -278.83) * mm, "end": v(300.74, -316.42) * mm});
            skLineSegment(sketch, "E43.0.6.8", {"start": v(394.72, -278.83) * mm, "end": v(357.12, -278.83) * mm});
            skLineSegment(sketch, "E43.3.6.8", {"start": v(357.12, -316.42) * mm, "end": v(394.72, -316.42) * mm});
            skLineSegment(sketch, "E43.6.6.8", {"start": v(394.72, -316.42) * mm, "end": v(394.72, -278.83) * mm});
            skLineSegment(sketch, "E43.9.6.8", {"start": v(357.12, -278.83) * mm, "end": v(357.12, -316.42) * mm});
            skLineSegment(sketch, "E43.0.7.8", {"start": v(451.1, -278.83) * mm, "end": v(413.51, -278.83) * mm});
            skLineSegment(sketch, "E43.3.7.8", {"start": v(413.51, -316.42) * mm, "end": v(451.1, -316.42) * mm});
            skLineSegment(sketch, "E43.6.7.8", {"start": v(451.1, -316.42) * mm, "end": v(451.1, -278.83) * mm});
            skLineSegment(sketch, "E43.9.7.8", {"start": v(413.51, -278.83) * mm, "end": v(413.51, -316.42) * mm});
            skLineSegment(sketch, "E44.0", {"start": v(338.33, -335.22) * mm, "end": v(244.35, -335.22) * mm});
            skLineSegment(sketch, "E44.1", {"start": v(451.1, -335.22) * mm, "end": v(357.12, -335.22) * mm});
            skLineSegment(sketch, "E44.2", {"start": v(244.35, -335.22) * mm, "end": v(244.35, -410.4) * mm});
            skLineSegment(sketch, "E44.3", {"start": v(338.33, -410.4) * mm, "end": v(244.35, -410.4) * mm});
            skLineSegment(sketch, "E44.4", {"start": v(338.33, -335.22) * mm, "end": v(338.33, -410.4) * mm});
            skLineSegment(sketch, "E44.5", {"start": v(357.12, -335.22) * mm, "end": v(357.12, -410.4) * mm});
            skLineSegment(sketch, "E44.6", {"start": v(451.1, -410.4) * mm, "end": v(357.12, -410.4) * mm});
            skLineSegment(sketch, "E44.7", {"start": v(451.1, -335.22) * mm, "end": v(451.1, -410.4) * mm});
            skPoint(sketch, "E45.endSnap0", {"position": v(37.6, -203.64) * mm});
            skLineSegment(sketch, "E46", {"start": v(37.6, -222.44) * mm, "end": v(37.6, -466.79) * mm});
            skLineSegment(sketch, "E47", {"start": v(37.6, -222.44) * mm, "end": v(225.55, -222.44) * mm});
            skPoint(sketch, "E47.endSnap0", {"position": v(263.14, -222.44) * mm});
            skLineSegment(sketch, "E48", {"start": v(225.55, -222.44) * mm, "end": v(225.55, -466.79) * mm});
            skLineSegment(sketch, "E49", {"start": v(225.55, -466.79) * mm, "end": v(37.6, -466.79) * mm});
            skSolve(sketch);
        }
        {
            var Q0;
            Q0=makeQuery(id+"F13.imprint","IMPRINT",FACE,{"disambiguationData":[TD([[makeQuery(id+"F13.imprint","IMPRINT",EDGE,{"derivedFrom":sQuery(id+"F13.wireOp",EDGE,"E32.bottom")}),-1.0]])]});
            var Q1;
            Q1=makeQuery(id+"F13.imprint","IMPRINT",FACE,{"disambiguationData":[TD([[makeQuery(id+"F13.imprint","IMPRINT",EDGE,{"derivedFrom":sQuery(id+"F13.wireOp",EDGE,"E33.1.0.0")}),-1.0]])]});
            var Q2;
            Q2=makeQuery(id+"F13.imprint","IMPRINT",FACE,{"disambiguationData":[TD([[makeQuery(id+"F13.imprint","IMPRINT",EDGE,{"derivedFrom":sQuery(id+"F13.wireOp",EDGE,"E44.0")}),1.0]])]});
            var Q3;
            Q3=makeQuery(id+"F13.imprint","IMPRINT",FACE,{"disambiguationData":[TD([[makeQuery(id+"F13.imprint","IMPRINT",EDGE,{"derivedFrom":sQuery(id+"F13.wireOp",EDGE,"E44.1")}),1.0]])]});
            extrude(context, id + "F14", {"entities" : qUnion([Q0, Q1, Q2, Q3]), "operationType" : NewBodyOperationType.REMOVE, "oppositeDirection" : true, "depth" : 19.05 * mm});
        }
        {
            var Q0;
            Q0 = qSketchRegion(id + "F13", true);
            extrude(context, id + "F15", {"entities" : qUnion([Q0]), "operationType" : NewBodyOperationType.REMOVE, "oppositeDirection" : true, "depth" : 6.35 * mm});
        }
        {
            var Q0;
            Q0=makeQuery(id+"F1.opExtrude","SWEPT_FACE",FACE,{"disambiguationData":[OSD([sQuery(id+"F0.wireOp",EDGE,"E3")])]});
            var sketch = newSketch(context, id + "F16", { "sketchPlane" : qUnion([Q0])});
            skLineSegment(sketch, "E50.0", {"start": v(244.35, 266.26) * mm, "end": v(244.35, 191.07) * mm});
            skLineSegment(sketch, "E51.0", {"start": v(338.33, 266.26) * mm, "end": v(244.35, 266.26) * mm});
            skLineSegment(sketch, "E52.0", {"start": v(338.33, 266.26) * mm, "end": v(338.33, 191.07) * mm});
            skLineSegment(sketch, "E53.0", {"start": v(338.33, 191.07) * mm, "end": v(244.35, 191.07) * mm});
            skLineSegment(sketch, "E54.0", {"start": v(357.12, 266.26) * mm, "end": v(357.12, 191.07) * mm});
            skLineSegment(sketch, "E55.0", {"start": v(451.1, 266.26) * mm, "end": v(357.12, 266.26) * mm});
            skLineSegment(sketch, "E56.0", {"start": v(451.1, 191.07) * mm, "end": v(357.12, 191.07) * mm});
            skLineSegment(sketch, "E57.0", {"start": v(451.1, 266.26) * mm, "end": v(451.1, 191.07) * mm});
            skLineSegment(sketch, "E58.0", {"start": v(300.74, 172.28) * mm, "end": v(300.74, 134.68) * mm});
            skLineSegment(sketch, "E59.0", {"start": v(338.33, 172.28) * mm, "end": v(338.33, 134.68) * mm});
            skLineSegment(sketch, "E60.0", {"start": v(338.33, 172.28) * mm, "end": v(300.74, 172.28) * mm});
            skLineSegment(sketch, "E61.0", {"start": v(338.33, 134.68) * mm, "end": v(300.74, 134.68) * mm});
            skLineSegment(sketch, "E62.0", {"start": v(281.94, 172.28) * mm, "end": v(281.94, 134.68) * mm});
            skLineSegment(sketch, "E63.0", {"start": v(281.94, 134.68) * mm, "end": v(244.35, 134.68) * mm});
            skLineSegment(sketch, "E64.0", {"start": v(244.35, 172.28) * mm, "end": v(244.35, 134.68) * mm});
            skLineSegment(sketch, "E65.0", {"start": v(281.94, 172.28) * mm, "end": v(244.35, 172.28) * mm});
            skLineSegment(sketch, "E66.0", {"start": v(357.12, 172.28) * mm, "end": v(357.12, 134.68) * mm});
            skLineSegment(sketch, "E67.0", {"start": v(394.72, 134.68) * mm, "end": v(357.12, 134.68) * mm});
            skLineSegment(sketch, "E68.0", {"start": v(394.72, 172.28) * mm, "end": v(357.12, 172.28) * mm});
            skLineSegment(sketch, "E69.0", {"start": v(394.72, 172.28) * mm, "end": v(394.72, 134.68) * mm});
            skLineSegment(sketch, "E70.0", {"start": v(413.51, 172.28) * mm, "end": v(413.51, 134.68) * mm});
            skLineSegment(sketch, "E71.0", {"start": v(451.1, 172.28) * mm, "end": v(413.51, 172.28) * mm});
            skLineSegment(sketch, "E72.0", {"start": v(451.1, 134.68) * mm, "end": v(413.51, 134.68) * mm});
            skLineSegment(sketch, "E73.0", {"start": v(451.1, 172.28) * mm, "end": v(451.1, 134.68) * mm});
            skLineSegment(sketch, "E74.0", {"start": v(451.1, 115.89) * mm, "end": v(413.51, 115.89) * mm});
            skLineSegment(sketch, "E75.0", {"start": v(413.51, 115.89) * mm, "end": v(413.51, 78.3) * mm});
            skLineSegment(sketch, "E76.0", {"start": v(451.1, 115.89) * mm, "end": v(451.1, 78.3) * mm});
            skLineSegment(sketch, "E77.0", {"start": v(451.1, 78.3) * mm, "end": v(413.51, 78.3) * mm});
            skLineSegment(sketch, "E78.0", {"start": v(451.1, 59.5) * mm, "end": v(413.51, 59.5) * mm});
            skLineSegment(sketch, "E79.0", {"start": v(451.1, 59.5) * mm, "end": v(451.1, 21.9) * mm});
            skLineSegment(sketch, "E80.0", {"start": v(451.1, 21.9) * mm, "end": v(413.51, 21.9) * mm});
            skLineSegment(sketch, "E81.0", {"start": v(413.51, 59.5) * mm, "end": v(413.51, 21.9) * mm});
            skLineSegment(sketch, "E82.0", {"start": v(394.72, 59.5) * mm, "end": v(394.72, 21.9) * mm});
            skLineSegment(sketch, "E83.0", {"start": v(394.72, 59.5) * mm, "end": v(357.12, 59.5) * mm});
            skLineSegment(sketch, "E84.0", {"start": v(357.12, 59.5) * mm, "end": v(357.12, 21.9) * mm});
            skLineSegment(sketch, "E85.0", {"start": v(394.72, 21.9) * mm, "end": v(357.12, 21.9) * mm});
            skLineSegment(sketch, "E86.0.0", {"start": v(469.9, 303.85) * mm, "end": v(244.35, 303.85) * mm});
            skLineSegment(sketch, "E86.0.1", {"start": v(244.35, 303.85) * mm, "end": v(244.35, 21.9) * mm});
            skLineSegment(sketch, "E86.0.2", {"start": v(244.35, 21.9) * mm, "end": v(469.9, 21.9) * mm});
            skLineSegment(sketch, "E86.0.3", {"start": v(469.9, 21.9) * mm, "end": v(469.9, 303.85) * mm});
            skLineSegment(sketch, "E87.0", {"start": v(394.72, 78.3) * mm, "end": v(357.12, 78.3) * mm});
            skLineSegment(sketch, "E88.0", {"start": v(394.72, 115.89) * mm, "end": v(394.72, 78.3) * mm});
            skLineSegment(sketch, "E89.0", {"start": v(394.72, 115.89) * mm, "end": v(357.12, 115.89) * mm});
            skLineSegment(sketch, "E90.0", {"start": v(357.12, 115.89) * mm, "end": v(357.12, 78.3) * mm});
            skLineSegment(sketch, "E91.0", {"start": v(338.33, 115.89) * mm, "end": v(338.33, 78.3) * mm});
            skLineSegment(sketch, "E92.0", {"start": v(338.33, 115.89) * mm, "end": v(300.74, 115.89) * mm});
            skLineSegment(sketch, "E93.0", {"start": v(338.33, 78.3) * mm, "end": v(300.74, 78.3) * mm});
            skLineSegment(sketch, "E94.0", {"start": v(300.74, 115.89) * mm, "end": v(300.74, 78.3) * mm});
            skLineSegment(sketch, "E95.0", {"start": v(338.33, 59.5) * mm, "end": v(300.74, 59.5) * mm});
            skLineSegment(sketch, "E96.0", {"start": v(300.74, 59.5) * mm, "end": v(300.74, 21.9) * mm});
            skLineSegment(sketch, "E97.0", {"start": v(338.33, 59.5) * mm, "end": v(338.33, 21.9) * mm});
            skLineSegment(sketch, "E98.0", {"start": v(338.33, 21.9) * mm, "end": v(300.74, 21.9) * mm});
            skLineSegment(sketch, "E99.0", {"start": v(281.94, 59.5) * mm, "end": v(281.94, 21.9) * mm});
            skLineSegment(sketch, "E100.0", {"start": v(281.94, 59.5) * mm, "end": v(244.35, 59.5) * mm});
            skLineSegment(sketch, "E101.0", {"start": v(244.35, 59.5) * mm, "end": v(244.35, 21.9) * mm});
            skLineSegment(sketch, "E102.0", {"start": v(281.94, 21.9) * mm, "end": v(244.35, 21.9) * mm});
            skLineSegment(sketch, "E103.0", {"start": v(281.94, 78.3) * mm, "end": v(244.35, 78.3) * mm});
            skLineSegment(sketch, "E104.0", {"start": v(281.94, 115.89) * mm, "end": v(281.94, 78.3) * mm});
            skLineSegment(sketch, "E105.0", {"start": v(244.35, 115.89) * mm, "end": v(244.35, 78.3) * mm});
            skLineSegment(sketch, "E106.0", {"start": v(281.94, 115.89) * mm, "end": v(244.35, 115.89) * mm});
            skSolve(sketch);
        }
        {
            var Q0;
            Q0=makeQuery(id+"F16.imprint","IMPRINT",FACE,{"disambiguationData":[TD([[makeQuery(id+"F16.imprint","IMPRINT",EDGE,{"derivedFrom":sQuery(id+"F16.wireOp",EDGE,"E54.0")}),1.0]])]});
            var Q1;
            {var subQ0=sQuery(id+"F16.wireOp",EDGE,"E51.0");Q1=makeQuery(id+"F16.imprint","IMPRINT",FACE,{"disambiguationData":[TD([[makeQuery(id+"F16.imprint","IMPRINT",EDGE,{"derivedFrom":subQ0}),1.0]])]});}
            extrude(context, id + "F17", {"entities" : qUnion([Q0, Q1]), "operationType" : NewBodyOperationType.REMOVE, "oppositeDirection" : true, "depth" : 19.05 * mm});
        }
        {
            var Q0;
            Q0=makeQuery(id+"F16.imprint","IMPRINT",FACE,{"disambiguationData":[TD([[makeQuery(id+"F16.imprint","IMPRINT",EDGE,{"derivedFrom":sQuery(id+"F16.wireOp",EDGE,"E62.0")}),-1.0]])]});
            var Q1;
            Q1=makeQuery(id+"F16.imprint","IMPRINT",FACE,{"disambiguationData":[TD([[makeQuery(id+"F16.imprint","IMPRINT",EDGE,{"derivedFrom":sQuery(id+"F16.wireOp",EDGE,"E103.0")}),-1.0]])]});
            var Q2;
            Q2=makeQuery(id+"F16.imprint","IMPRINT",FACE,{"disambiguationData":[TD([[makeQuery(id+"F16.imprint","IMPRINT",EDGE,{"derivedFrom":sQuery(id+"F16.wireOp",EDGE,"E99.0")}),-1.0]])]});
            var Q3;
            Q3=makeQuery(id+"F16.imprint","IMPRINT",FACE,{"disambiguationData":[TD([[makeQuery(id+"F16.imprint","IMPRINT",EDGE,{"derivedFrom":sQuery(id+"F16.wireOp",EDGE,"E95.0")}),1.0]])]});
            var Q4;
            Q4=makeQuery(id+"F16.imprint","IMPRINT",FACE,{"disambiguationData":[TD([[makeQuery(id+"F16.imprint","IMPRINT",EDGE,{"derivedFrom":sQuery(id+"F16.wireOp",EDGE,"E91.0")}),-1.0]])]});
            var Q5;
            Q5=makeQuery(id+"F16.imprint","IMPRINT",FACE,{"disambiguationData":[TD([[makeQuery(id+"F16.imprint","IMPRINT",EDGE,{"derivedFrom":sQuery(id+"F16.wireOp",EDGE,"E58.0")}),1.0]])]});
            var Q6;
            Q6=makeQuery(id+"F16.imprint","IMPRINT",FACE,{"disambiguationData":[TD([[makeQuery(id+"F16.imprint","IMPRINT",EDGE,{"derivedFrom":sQuery(id+"F16.wireOp",EDGE,"E66.0")}),1.0]])]});
            var Q7;
            Q7=makeQuery(id+"F16.imprint","IMPRINT",FACE,{"disambiguationData":[TD([[makeQuery(id+"F16.imprint","IMPRINT",EDGE,{"derivedFrom":sQuery(id+"F16.wireOp",EDGE,"E87.0")}),-1.0]])]});
            var Q8;
            {var subQ0=sQuery(id+"F16.wireOp",EDGE,"E82.0");Q8=makeQuery(id+"F16.imprint","IMPRINT",FACE,{"disambiguationData":[TD([[makeQuery(id+"F16.imprint","IMPRINT",EDGE,{"derivedFrom":subQ0}),-1.0]])]});}
            var Q9;
            Q9=makeQuery(id+"F16.imprint","IMPRINT",FACE,{"disambiguationData":[TD([[makeQuery(id+"F16.imprint","IMPRINT",EDGE,{"derivedFrom":sQuery(id+"F16.wireOp",EDGE,"E78.0")}),1.0]])]});
            var Q10;
            Q10=makeQuery(id+"F16.imprint","IMPRINT",FACE,{"disambiguationData":[TD([[makeQuery(id+"F16.imprint","IMPRINT",EDGE,{"derivedFrom":sQuery(id+"F16.wireOp",EDGE,"E74.0")}),1.0]])]});
            var Q11;
            Q11=makeQuery(id+"F16.imprint","IMPRINT",FACE,{"disambiguationData":[TD([[makeQuery(id+"F16.imprint","IMPRINT",EDGE,{"derivedFrom":sQuery(id+"F16.wireOp",EDGE,"E70.0")}),1.0]])]});
            var Q12;
            Q12=makeQuery(id+"F16.imprint","IMPRINT",FACE,{"disambiguationData":[TD([[makeQuery(id+"F16.imprint","IMPRINT",EDGE,{"derivedFrom":sQuery(id+"F16.wireOp",EDGE,"E54.0")}),1.0]])]});
            var Q13;
            {var subQ0=sQuery(id+"F16.wireOp",EDGE,"E51.0");Q13=makeQuery(id+"F16.imprint","IMPRINT",FACE,{"disambiguationData":[TD([[makeQuery(id+"F16.imprint","IMPRINT",EDGE,{"derivedFrom":subQ0}),1.0]])]});}
            extrude(context, id + "F18", {"entities" : qUnion([Q0, Q1, Q2, Q3, Q4, Q5, Q6, Q7, Q8, Q9, Q10, Q11, Q12, Q13]), "operationType" : NewBodyOperationType.REMOVE, "oppositeDirection" : true, "depth" : 6.35 * mm});
        }
        {
            var Q0;
            Q0=makeQuery(id+"F3.opExtrude","SWEPT_FACE",FACE,{"disambiguationData":[OSD([sQuery(id+"F2.wireOp",EDGE,"E6")])]});
            var sketch = newSketch(context, id + "F19", { "sketchPlane" : qUnion([Q0])});
            skLineSegment(sketch, "E107.0", {"start": v(334.75, 266.26) * mm, "end": v(240.77, 266.26) * mm});
            skLineSegment(sketch, "E108.0", {"start": v(240.77, 266.26) * mm, "end": v(240.77, 191.07) * mm});
            skLineSegment(sketch, "E108.1", {"start": v(334.75, 266.26) * mm, "end": v(334.75, 191.07) * mm});
            skLineSegment(sketch, "E108.2", {"start": v(334.75, 191.07) * mm, "end": v(240.77, 191.07) * mm});
            skLineSegment(sketch, "E109.0", {"start": v(221.98, 266.26) * mm, "end": v(128, 266.26) * mm});
            skLineSegment(sketch, "E109.1", {"start": v(221.98, 266.26) * mm, "end": v(221.98, 191.07) * mm});
            skLineSegment(sketch, "E109.2", {"start": v(221.98, 191.07) * mm, "end": v(128, 191.07) * mm});
            skLineSegment(sketch, "E109.3", {"start": v(128, 266.26) * mm, "end": v(128, 191.07) * mm});
            skLineSegment(sketch, "E110.0", {"start": v(128, 172.28) * mm, "end": v(128, 134.68) * mm});
            skLineSegment(sketch, "E111.0", {"start": v(165.59, 172.28) * mm, "end": v(128, 172.28) * mm});
            skLineSegment(sketch, "E112.0", {"start": v(165.59, 172.28) * mm, "end": v(165.59, 134.68) * mm});
            skLineSegment(sketch, "E113.0", {"start": v(165.59, 134.68) * mm, "end": v(128, 134.68) * mm});
            skLineSegment(sketch, "E114.0", {"start": v(184.39, 172.28) * mm, "end": v(184.39, 134.68) * mm});
            skLineSegment(sketch, "E115.0", {"start": v(221.98, 172.28) * mm, "end": v(184.39, 172.28) * mm});
            skLineSegment(sketch, "E116.0", {"start": v(221.98, 172.28) * mm, "end": v(221.98, 134.68) * mm});
            skLineSegment(sketch, "E117.0", {"start": v(221.98, 134.68) * mm, "end": v(184.39, 134.68) * mm});
            skLineSegment(sketch, "E118.0", {"start": v(240.77, 172.28) * mm, "end": v(240.77, 134.68) * mm});
            skLineSegment(sketch, "E119.0", {"start": v(278.37, 172.28) * mm, "end": v(240.77, 172.28) * mm});
            skLineSegment(sketch, "E120.0", {"start": v(278.37, 172.28) * mm, "end": v(278.37, 134.68) * mm});
            skLineSegment(sketch, "E121.0", {"start": v(278.37, 134.68) * mm, "end": v(240.77, 134.68) * mm});
            skLineSegment(sketch, "E122.0", {"start": v(334.75, 134.68) * mm, "end": v(297.16, 134.68) * mm});
            skLineSegment(sketch, "E123.0", {"start": v(297.16, 172.28) * mm, "end": v(297.16, 134.68) * mm});
            skLineSegment(sketch, "E124.0", {"start": v(334.75, 172.28) * mm, "end": v(297.16, 172.28) * mm});
            skLineSegment(sketch, "E125.0", {"start": v(334.75, 172.28) * mm, "end": v(334.75, 134.68) * mm});
            skLineSegment(sketch, "E126.0", {"start": v(334.75, 115.89) * mm, "end": v(334.75, 78.3) * mm});
            skLineSegment(sketch, "E127.0", {"start": v(334.75, 115.89) * mm, "end": v(297.16, 115.89) * mm});
            skLineSegment(sketch, "E128.0", {"start": v(297.16, 115.89) * mm, "end": v(297.16, 78.3) * mm});
            skLineSegment(sketch, "E129.0", {"start": v(334.75, 78.3) * mm, "end": v(297.16, 78.3) * mm});
            skLineSegment(sketch, "E130.0", {"start": v(278.37, 115.89) * mm, "end": v(278.37, 78.3) * mm});
            skLineSegment(sketch, "E131.0", {"start": v(278.37, 115.89) * mm, "end": v(240.77, 115.89) * mm});
            skLineSegment(sketch, "E132.0", {"start": v(278.37, 78.3) * mm, "end": v(240.77, 78.3) * mm});
            skLineSegment(sketch, "E133.0", {"start": v(240.77, 115.89) * mm, "end": v(240.77, 78.3) * mm});
            skLineSegment(sketch, "E134.0", {"start": v(221.98, 115.89) * mm, "end": v(221.98, 78.3) * mm});
            skLineSegment(sketch, "E135.0", {"start": v(221.98, 115.89) * mm, "end": v(184.39, 115.89) * mm});
            skLineSegment(sketch, "E136.0", {"start": v(221.98, 78.3) * mm, "end": v(184.39, 78.3) * mm});
            skLineSegment(sketch, "E137.0", {"start": v(184.39, 115.89) * mm, "end": v(184.39, 78.3) * mm});
            skLineSegment(sketch, "E138.0", {"start": v(165.59, 115.89) * mm, "end": v(165.59, 78.3) * mm});
            skLineSegment(sketch, "E139.0", {"start": v(165.59, 115.89) * mm, "end": v(128, 115.89) * mm});
            skLineSegment(sketch, "E140.0", {"start": v(128, 115.89) * mm, "end": v(128, 78.3) * mm});
            skLineSegment(sketch, "E141.0", {"start": v(165.59, 78.3) * mm, "end": v(128, 78.3) * mm});
            skLineSegment(sketch, "E142.0", {"start": v(165.59, 59.5) * mm, "end": v(128, 59.5) * mm});
            skLineSegment(sketch, "E143.0", {"start": v(128, 59.5) * mm, "end": v(128, 21.9) * mm});
            skLineSegment(sketch, "E144.0", {"start": v(165.59, 59.5) * mm, "end": v(165.59, 21.9) * mm});
            skLineSegment(sketch, "E145.0", {"start": v(165.59, 21.9) * mm, "end": v(128, 21.9) * mm});
            skLineSegment(sketch, "E146.0", {"start": v(221.98, 21.9) * mm, "end": v(184.39, 21.9) * mm});
            skLineSegment(sketch, "E147.0", {"start": v(184.39, 59.5) * mm, "end": v(184.39, 21.9) * mm});
            skLineSegment(sketch, "E148.0", {"start": v(221.98, 59.5) * mm, "end": v(184.39, 59.5) * mm});
            skLineSegment(sketch, "E149.0", {"start": v(221.98, 59.5) * mm, "end": v(221.98, 21.9) * mm});
            skLineSegment(sketch, "E150.0", {"start": v(240.77, 59.5) * mm, "end": v(240.77, 21.9) * mm});
            skLineSegment(sketch, "E151.0", {"start": v(278.37, 59.5) * mm, "end": v(240.77, 59.5) * mm});
            skLineSegment(sketch, "E152.0", {"start": v(278.37, 59.5) * mm, "end": v(278.37, 21.9) * mm});
            skLineSegment(sketch, "E153.0", {"start": v(278.37, 21.9) * mm, "end": v(240.77, 21.9) * mm});
            skLineSegment(sketch, "E154.0", {"start": v(297.16, 59.5) * mm, "end": v(297.16, 21.9) * mm});
            skLineSegment(sketch, "E155.0", {"start": v(334.75, 59.5) * mm, "end": v(297.16, 59.5) * mm});
            skLineSegment(sketch, "E156.0", {"start": v(334.75, 59.5) * mm, "end": v(334.75, 21.9) * mm});
            skLineSegment(sketch, "E157.0", {"start": v(334.75, 21.9) * mm, "end": v(297.16, 21.9) * mm});
            skSolve(sketch);
        }
        {
            var Q0;
            Q0=makeQuery(id+"F19.imprint","IMPRINT",FACE,{"disambiguationData":[TD([[makeQuery(id+"F19.imprint","IMPRINT",EDGE,{"derivedFrom":sQuery(id+"F19.wireOp",EDGE,"E109.0")}),1.0]])]});
            var Q1;
            Q1=makeQuery(id+"F19.imprint","IMPRINT",FACE,{"disambiguationData":[TD([[makeQuery(id+"F19.imprint","IMPRINT",EDGE,{"derivedFrom":sQuery(id+"F19.wireOp",EDGE,"E107.0")}),1.0]])]});
            extrude(context, id + "F20", {"entities" : qUnion([Q0, Q1]), "operationType" : NewBodyOperationType.REMOVE, "oppositeDirection" : true, "depth" : 19.05 * mm});
        }
        {
            var Q0;
            Q0=makeQuery(id+"F7.imprint","IMPRINT",FACE,{"disambiguationData":[TD([[makeQuery(id+"F7.imprint","IMPRINT",EDGE,{"derivedFrom":sQuery(id+"F7.wireOp",EDGE,"E17.bottom")}),-1.0]])]});
            extrude(context, id + "F21", {"entities" : qUnion([Q0]), "operationType" : NewBodyOperationType.REMOVE, "oppositeDirection" : true, "depth" : 224.03 * mm});
        }
        {
            var Q0;
            Q0=makeQuery(id+"F13.imprint","IMPRINT",FACE,{"disambiguationData":[TD([[makeQuery(id+"F13.imprint","IMPRINT",EDGE,{"derivedFrom":sQuery(id+"F13.wireOp",EDGE,"E46")}),1.0]])]});
            extrude(context, id + "F22", {"entities" : qUnion([Q0]), "operationType" : NewBodyOperationType.REMOVE, "oppositeDirection" : true, "depth" : 223.52 * mm});
        }
        {
            var Q0;
            Q0=makeQuery(id+"F19.imprint","IMPRINT",FACE,{"disambiguationData":[TD([[makeQuery(id+"F19.imprint","IMPRINT",EDGE,{"derivedFrom":sQuery(id+"F19.wireOp",EDGE,"E110.0")}),1.0]])]});
            var Q1;
            Q1=makeQuery(id+"F19.imprint","IMPRINT",FACE,{"disambiguationData":[TD([[makeQuery(id+"F19.imprint","IMPRINT",EDGE,{"derivedFrom":sQuery(id+"F19.wireOp",EDGE,"E114.0")}),1.0]])]});
            var Q2;
            Q2=makeQuery(id+"F19.imprint","IMPRINT",FACE,{"disambiguationData":[TD([[makeQuery(id+"F19.imprint","IMPRINT",EDGE,{"derivedFrom":sQuery(id+"F19.wireOp",EDGE,"E118.0")}),1.0]])]});
            var Q3;
            Q3=makeQuery(id+"F19.imprint","IMPRINT",FACE,{"disambiguationData":[TD([[makeQuery(id+"F19.imprint","IMPRINT",EDGE,{"derivedFrom":sQuery(id+"F19.wireOp",EDGE,"E122.0")}),-1.0]])]});
            var Q4;
            Q4=makeQuery(id+"F19.imprint","IMPRINT",FACE,{"disambiguationData":[TD([[makeQuery(id+"F19.imprint","IMPRINT",EDGE,{"derivedFrom":sQuery(id+"F19.wireOp",EDGE,"E126.0")}),-1.0]])]});
            var Q5;
            Q5=makeQuery(id+"F19.imprint","IMPRINT",FACE,{"disambiguationData":[TD([[makeQuery(id+"F19.imprint","IMPRINT",EDGE,{"derivedFrom":sQuery(id+"F19.wireOp",EDGE,"E130.0")}),-1.0]])]});
            var Q6;
            Q6=makeQuery(id+"F19.imprint","IMPRINT",FACE,{"disambiguationData":[TD([[makeQuery(id+"F19.imprint","IMPRINT",EDGE,{"derivedFrom":sQuery(id+"F19.wireOp",EDGE,"E134.0")}),-1.0]])]});
            var Q7;
            Q7=makeQuery(id+"F19.imprint","IMPRINT",FACE,{"disambiguationData":[TD([[makeQuery(id+"F19.imprint","IMPRINT",EDGE,{"derivedFrom":sQuery(id+"F19.wireOp",EDGE,"E138.0")}),-1.0]])]});
            var Q8;
            Q8=makeQuery(id+"F19.imprint","IMPRINT",FACE,{"disambiguationData":[TD([[makeQuery(id+"F19.imprint","IMPRINT",EDGE,{"derivedFrom":sQuery(id+"F19.wireOp",EDGE,"E142.0")}),1.0]])]});
            var Q9;
            Q9=makeQuery(id+"F19.imprint","IMPRINT",FACE,{"disambiguationData":[TD([[makeQuery(id+"F19.imprint","IMPRINT",EDGE,{"derivedFrom":sQuery(id+"F19.wireOp",EDGE,"E146.0")}),1.0]])]});
            var Q10;
            Q10=makeQuery(id+"F19.imprint","IMPRINT",FACE,{"disambiguationData":[TD([[makeQuery(id+"F19.imprint","IMPRINT",EDGE,{"derivedFrom":sQuery(id+"F19.wireOp",EDGE,"E150.0")}),1.0]])]});
            var Q11;
            Q11=makeQuery(id+"F19.imprint","IMPRINT",FACE,{"disambiguationData":[TD([[makeQuery(id+"F19.imprint","IMPRINT",EDGE,{"derivedFrom":sQuery(id+"F19.wireOp",EDGE,"E154.0")}),1.0]])]});
            var Q12;
            Q12=makeQuery(id+"F20.boolean.opBoolean","COPY",FACE,{"derivedFrom":makeQuery(id+"F20.opExtrude","CAP_FACE",FACE,{"disambiguationData":[OSD([sQuery(id+"F19.wireOp",EDGE,"E109.0"),sQuery(id+"F19.wireOp",EDGE,"E109.1"),sQuery(id+"F19.wireOp",EDGE,"E109.2"),sQuery(id+"F19.wireOp",EDGE,"E109.3")])],"isStart":false})});
            var Q13;
            Q13=makeQuery(id+"F20.boolean.opBoolean","COPY",FACE,{"derivedFrom":makeQuery(id+"F20.opExtrude","CAP_FACE",FACE,{"disambiguationData":[OSD([sQuery(id+"F19.wireOp",EDGE,"E107.0"),sQuery(id+"F19.wireOp",EDGE,"E108.0"),sQuery(id+"F19.wireOp",EDGE,"E108.1"),sQuery(id+"F19.wireOp",EDGE,"E108.2")])],"isStart":false})});
            extrude(context, id + "F23", {"entities" : qUnion([Q0, Q1, Q2, Q3, Q4, Q5, Q6, Q7, Q8, Q9, Q10, Q11, Q12, Q13]), "operationType" : NewBodyOperationType.REMOVE, "oppositeDirection" : true, "depth" : 6.35 * mm});
        }
        {
            var Q0;
            {var subQ4=sQuery(id+"F0.wireOp",EDGE,"E0");var subQ10=sQuery(id+"F0.wireOp",EDGE,"E1");Q0=makeQuery(id+"F22.boolean.opBoolean","SPLIT",FACE,{"disambiguationData":[TD([makeQuery(id+"F1.opExtrude","SWEPT_FACE",FACE,{"disambiguationData":[OSD([subQ10])]})])],"derivedFrom":makeQuery(id+"F1.opExtrude","SWEPT_FACE",FACE,{"disambiguationData":[OSD([subQ4])]})});}
            var Q1;
            {var subQ2=sQuery(id+"F0.wireOp",EDGE,"E0");var subQ3=sQuery(id+"F7.wireOp",EDGE,"E17.left");Q1=makeQuery(id+"F22.boolean.opBoolean","SPLIT",FACE,{"disambiguationData":[TD([makeQuery(id+"F9.boolean.opBoolean","COPY",FACE,{"derivedFrom":makeQuery(id+"F9.opExtrude","SWEPT_FACE",FACE,{"disambiguationData":[OSD([subQ3])]})})])],"derivedFrom":makeQuery(id+"F1.opExtrude","SWEPT_FACE",FACE,{"disambiguationData":[OSD([subQ2])]})});}
            extrude(context, id + "F24", {"entities" : qUnion([Q0, Q1]), "operationType" : NewBodyOperationType.REMOVE, "oppositeDirection" : true, "depth" : 18.8 * mm});
        }
        {
            var Q0;
            Q0=makeQuery(id+"F3.boolean.opBoolean","MERGE",FACE,{"derivedFrom":[makeQuery(id+"F1.opExtrude","SWEPT_FACE",FACE,{"disambiguationData":[OSD([sQuery(id+"F0.wireOp",EDGE,"E2")])]}),makeQuery(id+"F3.opExtrude","CAP_FACE",FACE,{"disambiguationData":[OSD([sQuery(id+"F0.wireOp",EDGE,"E3"),sQuery(id+"F0.wireOp",EDGE,"E4"),sQuery(id+"F0.wireOp",EDGE,"E5"),sQuery(id+"F2.wireOp",EDGE,"E6")])],"isStart":false})]});
            extrude(context, id + "F25", {"entities" : qUnion([Q0]), "operationType" : NewBodyOperationType.REMOVE, "oppositeDirection" : true, "depth" : 18.8 * mm});
        }
    });
